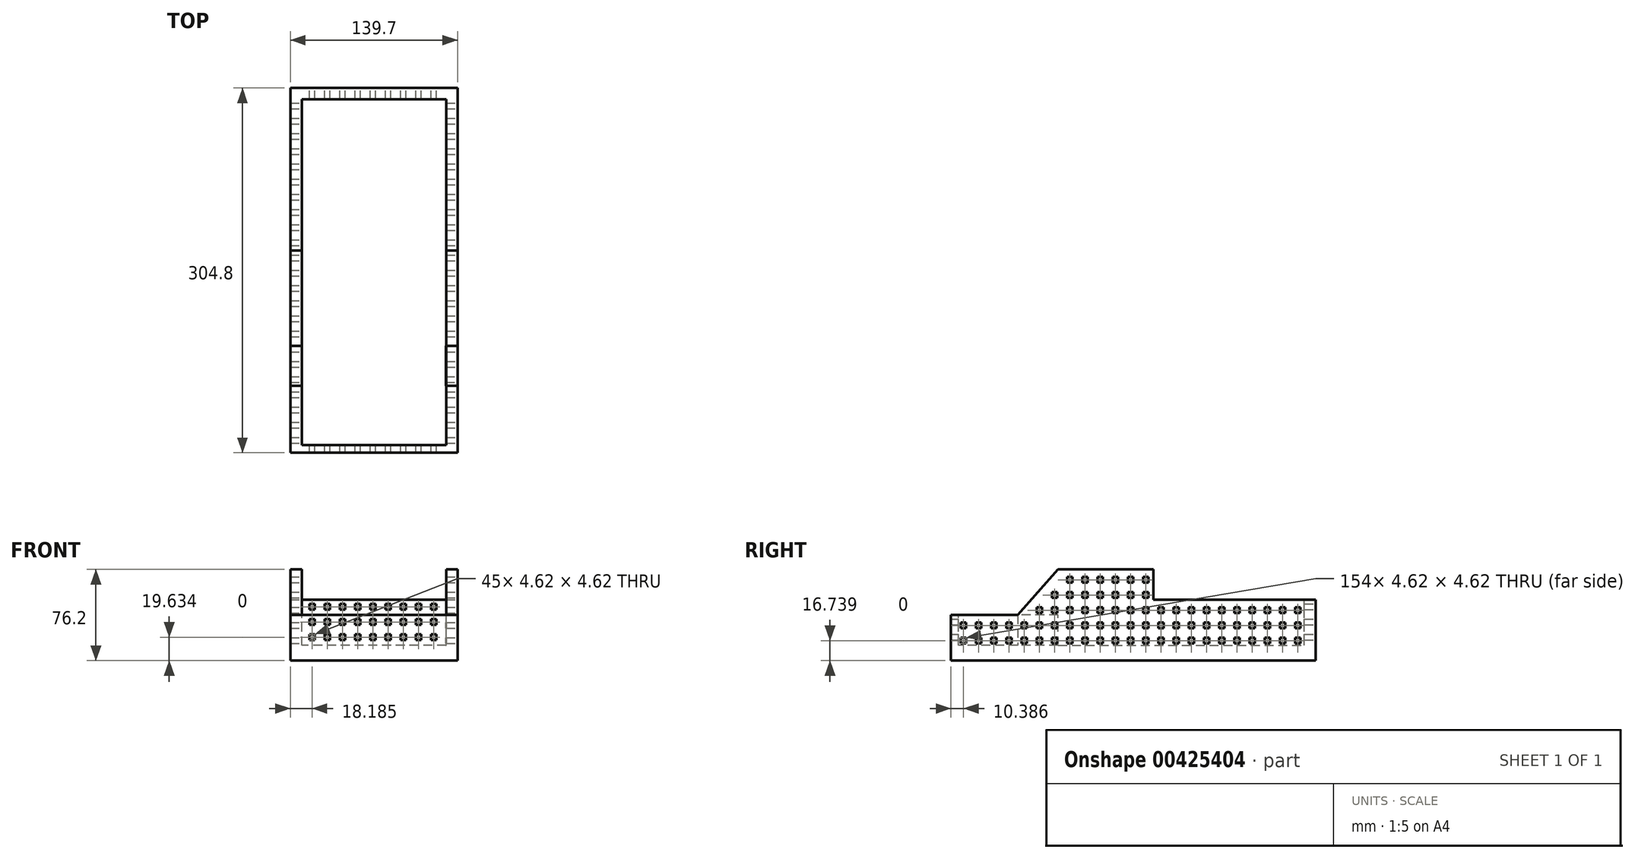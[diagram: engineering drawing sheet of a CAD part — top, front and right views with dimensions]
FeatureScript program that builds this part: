
annotation { "Feature Type Name" : "Feature", "Feature Type Description" : "" }
export const myFeature = defineFeature(function(context is Context, id is Id, definition is map)
    precondition{}
    {
        {
            var Q0;
            Q0=qCreatedBy(makeId("Top.planeOp"),FACE);
            var sketch = newSketch(context, id + "F0", { "sketchPlane" : qUnion([Q0])});
            skLineSegment(sketch, "E0.bottom", {"start": v(-57.73, 193.73) * mm, "end": v(81.97, 193.73) * mm});
            skLineSegment(sketch, "E0.top", {"start": v(-57.73, -111.07) * mm, "end": v(81.97, -111.07) * mm});
            skLineSegment(sketch, "E0.left", {"start": v(-57.73, 193.73) * mm, "end": v(-57.73, -111.07) * mm});
            skLineSegment(sketch, "E0.right", {"start": v(81.97, 193.73) * mm, "end": v(81.97, -111.07) * mm});
            skSolve(sketch);
        }
        {
            var Q0;
            Q0=makeQuery(id+"F0.imprint","IMPRINT",FACE,{"disambiguationData":[TD([[makeQuery(id+"F0.imprint","IMPRINT",EDGE,{"derivedFrom":sQuery(id+"F0.wireOp",EDGE,"E0.bottom")}),-1.0]])]});
            var Q1;
            Q1 = qSketchRegion(id + "F2", true);
            extrude(context, id + "F1", {"entities" : qUnion([Q0, Q1]), "oppositeDirection" : true, "depth" : 76.2 * mm});
        }
        {
            var Q0;
            Q0=makeQuery(id+"F1.opExtrude","SWEPT_FACE",FACE,{"disambiguationData":[OSD([sQuery(id+"F0.wireOp",EDGE,"E0.right")])]});
            var sketch = newSketch(context, id + "F2", { "sketchPlane" : qUnion([Q0])});
            skLineSegment(sketch, "E1", {"start": v(-111.07, -38.1) * mm, "end": v(-55.2, -38.1) * mm});
            skLineSegment(sketch, "E2", {"start": v(-55.2, -38.1) * mm, "end": v(-21.6, 0) * mm});
            skLineSegment(sketch, "E3", {"start": v(193.73, -25.4) * mm, "end": v(58.07, -25.4) * mm});
            skLineSegment(sketch, "E4", {"start": v(58.07, -25.4) * mm, "end": v(58.07, 0) * mm});
            skLineSegment(sketch, "E5", {"start": v(58.07, 0) * mm, "end": v(-21.6, 0) * mm});
            skSolve(sketch);
        }
        {
            var Q0;
            {var subQ0=sQuery(id+"F2.wireOp",EDGE,"E1");Q0=makeQuery(id+"F2.imprint","IMPRINT",FACE,{"disambiguationData":[TD([[makeQuery(id+"F2.imprint","IMPRINT",EDGE,{"derivedFrom":subQ0}),1.0]])]});}
            var Q1;
            {var subQ0=sQuery(id+"F2.wireOp",EDGE,"2gLDbXDt-uYVC-RE6O-0FNC-PgZezR3Lyq5D");Q1=makeQuery(id+"F2.imprint","IMPRINT",FACE,{"disambiguationData":[TD([[makeQuery(id+"F2.imprint","IMPRINT",EDGE,{"derivedFrom":subQ0}),-1.0]])]});}
            var Q2;
            {var subQ0=sQuery(id+"F2.wireOp",EDGE,"E3");Q2=makeQuery(id+"F2.imprint","IMPRINT",FACE,{"disambiguationData":[TD([[makeQuery(id+"F2.imprint","IMPRINT",EDGE,{"derivedFrom":subQ0}),-1.0]])]});}
            extrude(context, id + "F3", {"entities" : qUnion([Q0, Q1, Q2]), "operationType" : NewBodyOperationType.REMOVE, "endBound" : BoundingType.THROUGH_ALL, "oppositeDirection" : true, "depth" : 25.4 * mm});
        }
        {
            var Q0;
            Q0=makeQuery(id+"F3.boolean.opBoolean","COPY",FACE,{"derivedFrom":makeQuery(id+"F3.opExtrude","SWEPT_FACE",FACE,{"disambiguationData":[OSD([sQuery(id+"F2.wireOp",EDGE,"E3")])]})});
            var sketch = newSketch(context, id + "F4", { "sketchPlane" : qUnion([Q0])});
            skLineSegment(sketch, "E6.bottom", {"start": v(81.97, 58.07) * mm, "end": v(75.62, 58.07) * mm});
            skLineSegment(sketch, "E6.left", {"start": v(81.97, 58.07) * mm, "end": v(81.97, 64.42) * mm});
            skLineSegment(sketch, "E7.top", {"start": v(72.44, 184.2) * mm, "end": v(-48.2, 184.2) * mm});
            skLineSegment(sketch, "E7.left", {"start": v(72.44, 54.03) * mm, "end": v(72.44, 184.2) * mm});
            skLineSegment(sketch, "E7.right", {"start": v(-48.2, 54.03) * mm, "end": v(-48.2, 184.2) * mm});
            skSolve(sketch);
        }
        {
            var Q0;
            Q0=makeQuery(id+"F4.imprint","IMPRINT",FACE,{"disambiguationData":[TD([[makeQuery(id+"F4.imprint","IMPRINT",EDGE,{"derivedFrom":sQuery(id+"F4.wireOp",EDGE,"E7.bottom")}),-1.0]])]});
            var Q1;
            Q1=makeQuery(id+"F4.imprint","IMPRINT",FACE,{"disambiguationData":[TD([[makeQuery(id+"F4.imprint","IMPRINT",EDGE,{"derivedFrom":sQuery(id+"F4.wireOp",EDGE,"E7.top")}),1.0]])]});
            extrude(context, id + "F5", {"entities" : qUnion([Q0, Q1]), "operationType" : NewBodyOperationType.REMOVE, "oppositeDirection" : true, "depth" : 38.1 * mm});
        }
        {
            var Q0;
            Q0=makeQuery(id+"F1.opExtrude","CAP_FACE",FACE,{"disambiguationData":[OSD([sQuery(id+"F0.wireOp",EDGE,"E0.bottom"),sQuery(id+"F0.wireOp",EDGE,"E0.top"),sQuery(id+"F0.wireOp",EDGE,"E0.left"),sQuery(id+"F0.wireOp",EDGE,"E0.right")])],"isStart":true});
            var sketch = newSketch(context, id + "F6", { "sketchPlane" : qUnion([Q0])});
            skLineSegment(sketch, "E8.bottom", {"start": v(69.27, 58.07) * mm, "end": v(-45.03, 58.07) * mm});
            skLineSegment(sketch, "E8.top", {"start": v(69.27, -21.6) * mm, "end": v(-45.03, -21.6) * mm});
            skLineSegment(sketch, "E8.left", {"start": v(69.27, 58.07) * mm, "end": v(69.27, -21.6) * mm});
            skLineSegment(sketch, "E8.right", {"start": v(-45.03, 58.07) * mm, "end": v(-45.03, -21.6) * mm});
            skSolve(sketch);
        }
        {
            var Q0;
            Q0=makeQuery(id+"F6.imprint","IMPRINT",FACE,{"disambiguationData":[TD([[makeQuery(id+"F6.imprint","IMPRINT",EDGE,{"derivedFrom":sQuery(id+"F6.wireOp",EDGE,"E8.bottom")}),-1.0]])]});
            extrude(context, id + "F7", {"entities" : qUnion([Q0]), "operationType" : NewBodyOperationType.REMOVE, "oppositeDirection" : true, "depth" : 63.5 * mm});
        }
        {
            var Q0;
            Q0=makeQuery(id+"F3.boolean.opBoolean","COPY",FACE,{"derivedFrom":makeQuery(id+"F3.opExtrude","SWEPT_FACE",FACE,{"disambiguationData":[OSD([sQuery(id+"F2.wireOp",EDGE,"E1")])]})});
            var sketch = newSketch(context, id + "F8", { "sketchPlane" : qUnion([Q0])});
            skLineSegment(sketch, "E9.bottom", {"start": v(-57.73, -111.07) * mm, "end": v(-48.2, -111.07) * mm});
            skLineSegment(sketch, "E9.top", {"start": v(-57.73, -104.72) * mm, "end": v(-48.2, -104.72) * mm});
            skLineSegment(sketch, "E9.left", {"start": v(-57.73, -111.07) * mm, "end": v(-57.73, -104.72) * mm});
            skLineSegment(sketch, "E9.right", {"start": v(-48.2, -111.07) * mm, "end": v(-48.2, -104.72) * mm});
            skLineSegment(sketch, "E10.bottom", {"start": v(81.97, -55.2) * mm, "end": v(72.44, -55.2) * mm});
            skLineSegment(sketch, "E10.top", {"start": v(81.97, -61.54) * mm, "end": v(72.44, -61.54) * mm});
            skLineSegment(sketch, "E10.left", {"start": v(81.97, -55.2) * mm, "end": v(81.97, -61.54) * mm});
            skLineSegment(sketch, "E10.right", {"start": v(72.44, -55.2) * mm, "end": v(72.44, -61.54) * mm});
            skLineSegment(sketch, "E11.top", {"start": v(72.44, -104.72) * mm, "end": v(-48.2, -104.72) * mm});
            skLineSegment(sketch, "E11.left", {"start": v(72.44, -61.54) * mm, "end": v(72.44, -104.72) * mm});
            skLineSegment(sketch, "E11.right", {"start": v(-48.2, -61.54) * mm, "end": v(-48.2, -104.72) * mm});
            skLineSegment(sketch, "E12", {"start": v(-48.2, -61.54) * mm, "end": v(-48.2, -55.2) * mm});
            skSolve(sketch);
        }
        {
            var Q0;
            Q0=makeQuery(id+"F8.imprint","IMPRINT",FACE,{"disambiguationData":[TD([[makeQuery(id+"F8.imprint","IMPRINT",EDGE,{"derivedFrom":sQuery(id+"F8.wireOp",EDGE,"E11.bottom")}),1.0]])]});
            var Q1;
            {var subQ0=sQuery(id+"F8.wireOp",EDGE,"E10.right");Q1=makeQuery(id+"F8.imprint","IMPRINT",FACE,{"disambiguationData":[TD([[makeQuery(id+"F8.imprint","IMPRINT",EDGE,{"derivedFrom":subQ0}),-1.0]])]});}
            extrude(context, id + "F9", {"entities" : qUnion([Q0, Q1]), "operationType" : NewBodyOperationType.REMOVE, "oppositeDirection" : true, "depth" : 25.4 * mm});
        }
        {
            var Q0;
            Q0=makeQuery(id+"F1.opExtrude","SWEPT_FACE",FACE,{"disambiguationData":[OSD([sQuery(id+"F0.wireOp",EDGE,"E0.right")])]});
            var sketch = newSketch(context, id + "F10", { "sketchPlane" : qUnion([Q0])});
            skLineSegment(sketch, "E13.bottom", {"start": v(-111.07, -76.2) * mm, "end": v(-103, -76.2) * mm});
            skLineSegment(sketch, "E13.top", {"start": v(-111.07, -61.77) * mm, "end": v(-103, -61.77) * mm});
            skLineSegment(sketch, "E13.left", {"start": v(-111.07, -76.2) * mm, "end": v(-111.07, -61.77) * mm});
            skLineSegment(sketch, "E13.right", {"start": v(-103, -76.2) * mm, "end": v(-103, -61.77) * mm});
            skLineSegment(sketch, "E14.bottom", {"start": v(-103, -61.77) * mm, "end": v(-98.37, -61.77) * mm});
            skLineSegment(sketch, "E14.top", {"start": v(-103, -57.15) * mm, "end": v(-98.37, -57.15) * mm});
            skLineSegment(sketch, "E14.left", {"start": v(-103, -61.77) * mm, "end": v(-103, -57.15) * mm});
            skLineSegment(sketch, "E14.right", {"start": v(-98.37, -61.77) * mm, "end": v(-98.37, -57.15) * mm});
            skLineSegment(sketch, "E15.0.1.0", {"start": v(-98.37, -49.07) * mm, "end": v(-98.37, -44.45) * mm});
            skLineSegment(sketch, "E15.0.1.1", {"start": v(-103, -44.45) * mm, "end": v(-98.37, -44.45) * mm});
            skLineSegment(sketch, "E15.0.1.2", {"start": v(-103, -49.07) * mm, "end": v(-103, -44.45) * mm});
            skLineSegment(sketch, "E15.0.1.3", {"start": v(-103, -49.07) * mm, "end": v(-98.37, -49.07) * mm});
            skLineSegment(sketch, "E15.1.0.0", {"start": v(-85.67, -61.77) * mm, "end": v(-85.67, -57.15) * mm});
            skLineSegment(sketch, "E15.1.0.1", {"start": v(-90.3, -57.15) * mm, "end": v(-85.67, -57.15) * mm});
            skLineSegment(sketch, "E15.1.0.2", {"start": v(-90.3, -61.77) * mm, "end": v(-90.3, -57.15) * mm});
            skLineSegment(sketch, "E15.1.0.3", {"start": v(-90.3, -61.77) * mm, "end": v(-85.67, -61.77) * mm});
            skLineSegment(sketch, "E15.1.1.0", {"start": v(-85.67, -49.07) * mm, "end": v(-85.67, -44.45) * mm});
            skLineSegment(sketch, "E15.1.1.1", {"start": v(-90.3, -44.45) * mm, "end": v(-85.67, -44.45) * mm});
            skLineSegment(sketch, "E15.1.1.2", {"start": v(-90.3, -49.07) * mm, "end": v(-90.3, -44.45) * mm});
            skLineSegment(sketch, "E15.1.1.3", {"start": v(-90.3, -49.07) * mm, "end": v(-85.67, -49.07) * mm});
            skLineSegment(sketch, "E15.2.0.0", {"start": v(-72.97, -61.77) * mm, "end": v(-72.97, -57.15) * mm});
            skLineSegment(sketch, "E15.2.0.1", {"start": v(-77.6, -57.15) * mm, "end": v(-72.97, -57.15) * mm});
            skLineSegment(sketch, "E15.2.0.2", {"start": v(-77.6, -61.77) * mm, "end": v(-77.6, -57.15) * mm});
            skLineSegment(sketch, "E15.2.0.3", {"start": v(-77.6, -61.77) * mm, "end": v(-72.97, -61.77) * mm});
            skLineSegment(sketch, "E15.2.1.0", {"start": v(-72.97, -49.07) * mm, "end": v(-72.97, -44.45) * mm});
            skLineSegment(sketch, "E15.2.1.1", {"start": v(-77.6, -44.45) * mm, "end": v(-72.97, -44.45) * mm});
            skLineSegment(sketch, "E15.2.1.2", {"start": v(-77.6, -49.07) * mm, "end": v(-77.6, -44.45) * mm});
            skLineSegment(sketch, "E15.2.1.3", {"start": v(-77.6, -49.07) * mm, "end": v(-72.97, -49.07) * mm});
            skLineSegment(sketch, "E15.3.0.0", {"start": v(-60.27, -61.77) * mm, "end": v(-60.27, -57.15) * mm});
            skLineSegment(sketch, "E15.3.0.1", {"start": v(-64.9, -57.15) * mm, "end": v(-60.27, -57.15) * mm});
            skLineSegment(sketch, "E15.3.0.2", {"start": v(-64.9, -61.77) * mm, "end": v(-64.9, -57.15) * mm});
            skLineSegment(sketch, "E15.3.0.3", {"start": v(-64.9, -61.77) * mm, "end": v(-60.27, -61.77) * mm});
            skLineSegment(sketch, "E15.3.1.0", {"start": v(-60.27, -49.07) * mm, "end": v(-60.27, -44.45) * mm});
            skLineSegment(sketch, "E15.3.1.1", {"start": v(-64.9, -44.45) * mm, "end": v(-60.27, -44.45) * mm});
            skLineSegment(sketch, "E15.3.1.2", {"start": v(-64.9, -49.07) * mm, "end": v(-64.9, -44.45) * mm});
            skLineSegment(sketch, "E15.3.1.3", {"start": v(-64.9, -49.07) * mm, "end": v(-60.27, -49.07) * mm});
            skLineSegment(sketch, "E15.4.0.0", {"start": v(-47.57, -61.77) * mm, "end": v(-47.57, -57.15) * mm});
            skLineSegment(sketch, "E15.4.0.1", {"start": v(-52.2, -57.15) * mm, "end": v(-47.57, -57.15) * mm});
            skLineSegment(sketch, "E15.4.0.2", {"start": v(-52.2, -61.77) * mm, "end": v(-52.2, -57.15) * mm});
            skLineSegment(sketch, "E15.4.0.3", {"start": v(-52.2, -61.77) * mm, "end": v(-47.57, -61.77) * mm});
            skLineSegment(sketch, "E15.4.1.0", {"start": v(-47.57, -49.07) * mm, "end": v(-47.57, -44.45) * mm});
            skLineSegment(sketch, "E15.4.1.1", {"start": v(-52.2, -44.45) * mm, "end": v(-47.57, -44.45) * mm});
            skLineSegment(sketch, "E15.4.1.2", {"start": v(-52.2, -49.07) * mm, "end": v(-52.2, -44.45) * mm});
            skLineSegment(sketch, "E15.4.1.3", {"start": v(-52.2, -49.07) * mm, "end": v(-47.57, -49.07) * mm});
            skLineSegment(sketch, "E15.5.0.0", {"start": v(-34.87, -61.77) * mm, "end": v(-34.87, -57.15) * mm});
            skLineSegment(sketch, "E15.5.0.1", {"start": v(-39.5, -57.15) * mm, "end": v(-34.87, -57.15) * mm});
            skLineSegment(sketch, "E15.5.0.2", {"start": v(-39.5, -61.77) * mm, "end": v(-39.5, -57.15) * mm});
            skLineSegment(sketch, "E15.5.0.3", {"start": v(-39.5, -61.77) * mm, "end": v(-34.87, -61.77) * mm});
            skLineSegment(sketch, "E15.5.1.0", {"start": v(-34.87, -49.07) * mm, "end": v(-34.87, -44.45) * mm});
            skLineSegment(sketch, "E15.5.1.1", {"start": v(-39.5, -44.45) * mm, "end": v(-34.87, -44.45) * mm});
            skLineSegment(sketch, "E15.5.1.2", {"start": v(-39.5, -49.07) * mm, "end": v(-39.5, -44.45) * mm});
            skLineSegment(sketch, "E15.5.1.3", {"start": v(-39.5, -49.07) * mm, "end": v(-34.87, -49.07) * mm});
            skLineSegment(sketch, "E15.5.2.0", {"start": v(-34.87, -36.37) * mm, "end": v(-34.87, -31.75) * mm});
            skLineSegment(sketch, "E15.5.2.1", {"start": v(-39.5, -31.75) * mm, "end": v(-34.87, -31.75) * mm});
            skLineSegment(sketch, "E15.5.2.2", {"start": v(-39.5, -36.37) * mm, "end": v(-39.5, -31.75) * mm});
            skLineSegment(sketch, "E15.5.2.3", {"start": v(-39.5, -36.37) * mm, "end": v(-34.87, -36.37) * mm});
            skLineSegment(sketch, "E15.6.0.0", {"start": v(-22.17, -61.77) * mm, "end": v(-22.17, -57.15) * mm});
            skLineSegment(sketch, "E15.6.0.1", {"start": v(-26.8, -57.15) * mm, "end": v(-22.17, -57.15) * mm});
            skLineSegment(sketch, "E15.6.0.2", {"start": v(-26.8, -61.77) * mm, "end": v(-26.8, -57.15) * mm});
            skLineSegment(sketch, "E15.6.0.3", {"start": v(-26.8, -61.77) * mm, "end": v(-22.17, -61.77) * mm});
            skLineSegment(sketch, "E15.6.1.0", {"start": v(-22.17, -49.07) * mm, "end": v(-22.17, -44.45) * mm});
            skLineSegment(sketch, "E15.6.1.1", {"start": v(-26.8, -44.45) * mm, "end": v(-22.17, -44.45) * mm});
            skLineSegment(sketch, "E15.6.1.2", {"start": v(-26.8, -49.07) * mm, "end": v(-26.8, -44.45) * mm});
            skLineSegment(sketch, "E15.6.1.3", {"start": v(-26.8, -49.07) * mm, "end": v(-22.17, -49.07) * mm});
            skLineSegment(sketch, "E15.6.2.0", {"start": v(-22.17, -36.37) * mm, "end": v(-22.17, -31.75) * mm});
            skLineSegment(sketch, "E15.6.2.1", {"start": v(-26.8, -31.75) * mm, "end": v(-22.17, -31.75) * mm});
            skLineSegment(sketch, "E15.6.2.2", {"start": v(-26.8, -36.37) * mm, "end": v(-26.8, -31.75) * mm});
            skLineSegment(sketch, "E15.6.2.3", {"start": v(-26.8, -36.37) * mm, "end": v(-22.17, -36.37) * mm});
            skLineSegment(sketch, "E15.6.3.0", {"start": v(-22.17, -23.67) * mm, "end": v(-22.17, -19.05) * mm});
            skLineSegment(sketch, "E15.6.3.1", {"start": v(-26.8, -19.05) * mm, "end": v(-22.17, -19.05) * mm});
            skLineSegment(sketch, "E15.6.3.2", {"start": v(-26.8, -23.67) * mm, "end": v(-26.8, -19.05) * mm});
            skLineSegment(sketch, "E15.6.3.3", {"start": v(-26.8, -23.67) * mm, "end": v(-22.17, -23.67) * mm});
            skLineSegment(sketch, "E15.7.0.0", {"start": v(-9.47, -61.77) * mm, "end": v(-9.47, -57.15) * mm});
            skLineSegment(sketch, "E15.7.0.1", {"start": v(-14.1, -57.15) * mm, "end": v(-9.47, -57.15) * mm});
            skLineSegment(sketch, "E15.7.0.2", {"start": v(-14.1, -61.77) * mm, "end": v(-14.1, -57.15) * mm});
            skLineSegment(sketch, "E15.7.0.3", {"start": v(-14.1, -61.77) * mm, "end": v(-9.47, -61.77) * mm});
            skLineSegment(sketch, "E15.7.1.0", {"start": v(-9.47, -49.07) * mm, "end": v(-9.47, -44.45) * mm});
            skLineSegment(sketch, "E15.7.1.1", {"start": v(-14.1, -44.45) * mm, "end": v(-9.47, -44.45) * mm});
            skLineSegment(sketch, "E15.7.1.2", {"start": v(-14.1, -49.07) * mm, "end": v(-14.1, -44.45) * mm});
            skLineSegment(sketch, "E15.7.1.3", {"start": v(-14.1, -49.07) * mm, "end": v(-9.47, -49.07) * mm});
            skLineSegment(sketch, "E15.7.2.0", {"start": v(-9.47, -36.37) * mm, "end": v(-9.47, -31.75) * mm});
            skLineSegment(sketch, "E15.7.2.1", {"start": v(-14.1, -31.75) * mm, "end": v(-9.47, -31.75) * mm});
            skLineSegment(sketch, "E15.7.2.2", {"start": v(-14.1, -36.37) * mm, "end": v(-14.1, -31.75) * mm});
            skLineSegment(sketch, "E15.7.2.3", {"start": v(-14.1, -36.37) * mm, "end": v(-9.47, -36.37) * mm});
            skLineSegment(sketch, "E15.7.3.0", {"start": v(-9.47, -23.67) * mm, "end": v(-9.47, -19.05) * mm});
            skLineSegment(sketch, "E15.7.3.1", {"start": v(-14.1, -19.05) * mm, "end": v(-9.47, -19.05) * mm});
            skLineSegment(sketch, "E15.7.3.2", {"start": v(-14.1, -23.67) * mm, "end": v(-14.1, -19.05) * mm});
            skLineSegment(sketch, "E15.7.3.3", {"start": v(-14.1, -23.67) * mm, "end": v(-9.47, -23.67) * mm});
            skLineSegment(sketch, "E15.7.4.0", {"start": v(-9.47, -10.97) * mm, "end": v(-9.47, -6.35) * mm});
            skLineSegment(sketch, "E15.7.4.1", {"start": v(-14.1, -6.35) * mm, "end": v(-9.47, -6.35) * mm});
            skLineSegment(sketch, "E15.7.4.2", {"start": v(-14.1, -10.97) * mm, "end": v(-14.1, -6.35) * mm});
            skLineSegment(sketch, "E15.7.4.3", {"start": v(-14.1, -10.97) * mm, "end": v(-9.47, -10.97) * mm});
            skLineSegment(sketch, "E15.8.0.0", {"start": v(3.23, -61.77) * mm, "end": v(3.23, -57.15) * mm});
            skLineSegment(sketch, "E15.8.0.1", {"start": v(-1.4, -57.15) * mm, "end": v(3.23, -57.15) * mm});
            skLineSegment(sketch, "E15.8.0.2", {"start": v(-1.4, -61.77) * mm, "end": v(-1.4, -57.15) * mm});
            skLineSegment(sketch, "E15.8.0.3", {"start": v(-1.4, -61.77) * mm, "end": v(3.23, -61.77) * mm});
            skLineSegment(sketch, "E15.8.1.0", {"start": v(3.23, -49.07) * mm, "end": v(3.23, -44.45) * mm});
            skLineSegment(sketch, "E15.8.1.1", {"start": v(-1.4, -44.45) * mm, "end": v(3.23, -44.45) * mm});
            skLineSegment(sketch, "E15.8.1.2", {"start": v(-1.4, -49.07) * mm, "end": v(-1.4, -44.45) * mm});
            skLineSegment(sketch, "E15.8.1.3", {"start": v(-1.4, -49.07) * mm, "end": v(3.23, -49.07) * mm});
            skLineSegment(sketch, "E15.8.2.0", {"start": v(3.23, -36.37) * mm, "end": v(3.23, -31.75) * mm});
            skLineSegment(sketch, "E15.8.2.1", {"start": v(-1.4, -31.75) * mm, "end": v(3.23, -31.75) * mm});
            skLineSegment(sketch, "E15.8.2.2", {"start": v(-1.4, -36.37) * mm, "end": v(-1.4, -31.75) * mm});
            skLineSegment(sketch, "E15.8.2.3", {"start": v(-1.4, -36.37) * mm, "end": v(3.23, -36.37) * mm});
            skLineSegment(sketch, "E15.8.3.0", {"start": v(3.23, -23.67) * mm, "end": v(3.23, -19.05) * mm});
            skLineSegment(sketch, "E15.8.3.1", {"start": v(-1.4, -19.05) * mm, "end": v(3.23, -19.05) * mm});
            skLineSegment(sketch, "E15.8.3.2", {"start": v(-1.4, -23.67) * mm, "end": v(-1.4, -19.05) * mm});
            skLineSegment(sketch, "E15.8.3.3", {"start": v(-1.4, -23.67) * mm, "end": v(3.23, -23.67) * mm});
            skLineSegment(sketch, "E15.8.4.0", {"start": v(3.23, -10.97) * mm, "end": v(3.23, -6.35) * mm});
            skLineSegment(sketch, "E15.8.4.1", {"start": v(-1.4, -6.35) * mm, "end": v(3.23, -6.35) * mm});
            skLineSegment(sketch, "E15.8.4.2", {"start": v(-1.4, -10.97) * mm, "end": v(-1.4, -6.35) * mm});
            skLineSegment(sketch, "E15.8.4.3", {"start": v(-1.4, -10.97) * mm, "end": v(3.23, -10.97) * mm});
            skLineSegment(sketch, "E15.9.0.0", {"start": v(15.93, -61.77) * mm, "end": v(15.93, -57.15) * mm});
            skLineSegment(sketch, "E15.9.0.1", {"start": v(11.3, -57.15) * mm, "end": v(15.93, -57.15) * mm});
            skLineSegment(sketch, "E15.9.0.2", {"start": v(11.3, -61.77) * mm, "end": v(11.3, -57.15) * mm});
            skLineSegment(sketch, "E15.9.0.3", {"start": v(11.3, -61.77) * mm, "end": v(15.93, -61.77) * mm});
            skLineSegment(sketch, "E15.9.1.0", {"start": v(15.93, -49.07) * mm, "end": v(15.93, -44.45) * mm});
            skLineSegment(sketch, "E15.9.1.1", {"start": v(11.3, -44.45) * mm, "end": v(15.93, -44.45) * mm});
            skLineSegment(sketch, "E15.9.1.2", {"start": v(11.3, -49.07) * mm, "end": v(11.3, -44.45) * mm});
            skLineSegment(sketch, "E15.9.1.3", {"start": v(11.3, -49.07) * mm, "end": v(15.93, -49.07) * mm});
            skLineSegment(sketch, "E15.9.2.0", {"start": v(15.93, -36.37) * mm, "end": v(15.93, -31.75) * mm});
            skLineSegment(sketch, "E15.9.2.1", {"start": v(11.3, -31.75) * mm, "end": v(15.93, -31.75) * mm});
            skLineSegment(sketch, "E15.9.2.2", {"start": v(11.3, -36.37) * mm, "end": v(11.3, -31.75) * mm});
            skLineSegment(sketch, "E15.9.2.3", {"start": v(11.3, -36.37) * mm, "end": v(15.93, -36.37) * mm});
            skLineSegment(sketch, "E15.9.3.0", {"start": v(15.93, -23.67) * mm, "end": v(15.93, -19.05) * mm});
            skLineSegment(sketch, "E15.9.3.1", {"start": v(11.3, -19.05) * mm, "end": v(15.93, -19.05) * mm});
            skLineSegment(sketch, "E15.9.3.2", {"start": v(11.3, -23.67) * mm, "end": v(11.3, -19.05) * mm});
            skLineSegment(sketch, "E15.9.3.3", {"start": v(11.3, -23.67) * mm, "end": v(15.93, -23.67) * mm});
            skLineSegment(sketch, "E15.9.4.0", {"start": v(15.93, -10.97) * mm, "end": v(15.93, -6.35) * mm});
            skLineSegment(sketch, "E15.9.4.1", {"start": v(11.3, -6.35) * mm, "end": v(15.93, -6.35) * mm});
            skLineSegment(sketch, "E15.9.4.2", {"start": v(11.3, -10.97) * mm, "end": v(11.3, -6.35) * mm});
            skLineSegment(sketch, "E15.9.4.3", {"start": v(11.3, -10.97) * mm, "end": v(15.93, -10.97) * mm});
            skLineSegment(sketch, "E15.10.0.0", {"start": v(28.63, -61.77) * mm, "end": v(28.63, -57.15) * mm});
            skLineSegment(sketch, "E15.10.0.1", {"start": v(24, -57.15) * mm, "end": v(28.63, -57.15) * mm});
            skLineSegment(sketch, "E15.10.0.2", {"start": v(24, -61.77) * mm, "end": v(24, -57.15) * mm});
            skLineSegment(sketch, "E15.10.0.3", {"start": v(24, -61.77) * mm, "end": v(28.63, -61.77) * mm});
            skLineSegment(sketch, "E15.10.1.0", {"start": v(28.63, -49.07) * mm, "end": v(28.63, -44.45) * mm});
            skLineSegment(sketch, "E15.10.1.1", {"start": v(24, -44.45) * mm, "end": v(28.63, -44.45) * mm});
            skLineSegment(sketch, "E15.10.1.2", {"start": v(24, -49.07) * mm, "end": v(24, -44.45) * mm});
            skLineSegment(sketch, "E15.10.1.3", {"start": v(24, -49.07) * mm, "end": v(28.63, -49.07) * mm});
            skLineSegment(sketch, "E15.10.2.0", {"start": v(28.63, -36.37) * mm, "end": v(28.63, -31.75) * mm});
            skLineSegment(sketch, "E15.10.2.1", {"start": v(24, -31.75) * mm, "end": v(28.63, -31.75) * mm});
            skLineSegment(sketch, "E15.10.2.2", {"start": v(24, -36.37) * mm, "end": v(24, -31.75) * mm});
            skLineSegment(sketch, "E15.10.2.3", {"start": v(24, -36.37) * mm, "end": v(28.63, -36.37) * mm});
            skLineSegment(sketch, "E15.10.3.0", {"start": v(28.63, -23.67) * mm, "end": v(28.63, -19.05) * mm});
            skLineSegment(sketch, "E15.10.3.1", {"start": v(24, -19.05) * mm, "end": v(28.63, -19.05) * mm});
            skLineSegment(sketch, "E15.10.3.2", {"start": v(24, -23.67) * mm, "end": v(24, -19.05) * mm});
            skLineSegment(sketch, "E15.10.3.3", {"start": v(24, -23.67) * mm, "end": v(28.63, -23.67) * mm});
            skLineSegment(sketch, "E15.10.4.0", {"start": v(28.63, -10.97) * mm, "end": v(28.63, -6.35) * mm});
            skLineSegment(sketch, "E15.10.4.1", {"start": v(24, -6.35) * mm, "end": v(28.63, -6.35) * mm});
            skLineSegment(sketch, "E15.10.4.2", {"start": v(24, -10.97) * mm, "end": v(24, -6.35) * mm});
            skLineSegment(sketch, "E15.10.4.3", {"start": v(24, -10.97) * mm, "end": v(28.63, -10.97) * mm});
            skLineSegment(sketch, "E15.11.0.0", {"start": v(41.33, -61.77) * mm, "end": v(41.33, -57.15) * mm});
            skLineSegment(sketch, "E15.11.0.1", {"start": v(36.7, -57.15) * mm, "end": v(41.33, -57.15) * mm});
            skLineSegment(sketch, "E15.11.0.2", {"start": v(36.7, -61.77) * mm, "end": v(36.7, -57.15) * mm});
            skLineSegment(sketch, "E15.11.0.3", {"start": v(36.7, -61.77) * mm, "end": v(41.33, -61.77) * mm});
            skLineSegment(sketch, "E15.11.1.0", {"start": v(41.33, -49.07) * mm, "end": v(41.33, -44.45) * mm});
            skLineSegment(sketch, "E15.11.1.1", {"start": v(36.7, -44.45) * mm, "end": v(41.33, -44.45) * mm});
            skLineSegment(sketch, "E15.11.1.2", {"start": v(36.7, -49.07) * mm, "end": v(36.7, -44.45) * mm});
            skLineSegment(sketch, "E15.11.1.3", {"start": v(36.7, -49.07) * mm, "end": v(41.33, -49.07) * mm});
            skLineSegment(sketch, "E15.11.2.0", {"start": v(41.33, -36.37) * mm, "end": v(41.33, -31.75) * mm});
            skLineSegment(sketch, "E15.11.2.1", {"start": v(36.7, -31.75) * mm, "end": v(41.33, -31.75) * mm});
            skLineSegment(sketch, "E15.11.2.2", {"start": v(36.7, -36.37) * mm, "end": v(36.7, -31.75) * mm});
            skLineSegment(sketch, "E15.11.2.3", {"start": v(36.7, -36.37) * mm, "end": v(41.33, -36.37) * mm});
            skLineSegment(sketch, "E15.11.3.0", {"start": v(41.33, -23.67) * mm, "end": v(41.33, -19.05) * mm});
            skLineSegment(sketch, "E15.11.3.1", {"start": v(36.7, -19.05) * mm, "end": v(41.33, -19.05) * mm});
            skLineSegment(sketch, "E15.11.3.2", {"start": v(36.7, -23.67) * mm, "end": v(36.7, -19.05) * mm});
            skLineSegment(sketch, "E15.11.3.3", {"start": v(36.7, -23.67) * mm, "end": v(41.33, -23.67) * mm});
            skLineSegment(sketch, "E15.11.4.0", {"start": v(41.33, -10.97) * mm, "end": v(41.33, -6.35) * mm});
            skLineSegment(sketch, "E15.11.4.1", {"start": v(36.7, -6.35) * mm, "end": v(41.33, -6.35) * mm});
            skLineSegment(sketch, "E15.11.4.2", {"start": v(36.7, -10.97) * mm, "end": v(36.7, -6.35) * mm});
            skLineSegment(sketch, "E15.11.4.3", {"start": v(36.7, -10.97) * mm, "end": v(41.33, -10.97) * mm});
            skLineSegment(sketch, "E15.12.0.0", {"start": v(54.03, -61.77) * mm, "end": v(54.03, -57.15) * mm});
            skLineSegment(sketch, "E15.12.0.1", {"start": v(49.4, -57.15) * mm, "end": v(54.03, -57.15) * mm});
            skLineSegment(sketch, "E15.12.0.2", {"start": v(49.4, -61.77) * mm, "end": v(49.4, -57.15) * mm});
            skLineSegment(sketch, "E15.12.0.3", {"start": v(49.4, -61.77) * mm, "end": v(54.03, -61.77) * mm});
            skLineSegment(sketch, "E15.12.1.0", {"start": v(54.03, -49.07) * mm, "end": v(54.03, -44.45) * mm});
            skLineSegment(sketch, "E15.12.1.1", {"start": v(49.4, -44.45) * mm, "end": v(54.03, -44.45) * mm});
            skLineSegment(sketch, "E15.12.1.2", {"start": v(49.4, -49.07) * mm, "end": v(49.4, -44.45) * mm});
            skLineSegment(sketch, "E15.12.1.3", {"start": v(49.4, -49.07) * mm, "end": v(54.03, -49.07) * mm});
            skLineSegment(sketch, "E15.12.2.0", {"start": v(54.03, -36.37) * mm, "end": v(54.03, -31.75) * mm});
            skLineSegment(sketch, "E15.12.2.1", {"start": v(49.4, -31.75) * mm, "end": v(54.03, -31.75) * mm});
            skLineSegment(sketch, "E15.12.2.2", {"start": v(49.4, -36.37) * mm, "end": v(49.4, -31.75) * mm});
            skLineSegment(sketch, "E15.12.2.3", {"start": v(49.4, -36.37) * mm, "end": v(54.03, -36.37) * mm});
            skLineSegment(sketch, "E15.13.0.0", {"start": v(66.73, -61.77) * mm, "end": v(66.73, -57.15) * mm});
            skLineSegment(sketch, "E15.13.0.1", {"start": v(62.1, -57.15) * mm, "end": v(66.73, -57.15) * mm});
            skLineSegment(sketch, "E15.13.0.2", {"start": v(62.1, -61.77) * mm, "end": v(62.1, -57.15) * mm});
            skLineSegment(sketch, "E15.13.0.3", {"start": v(62.1, -61.77) * mm, "end": v(66.73, -61.77) * mm});
            skLineSegment(sketch, "E15.13.1.0", {"start": v(66.73, -49.07) * mm, "end": v(66.73, -44.45) * mm});
            skLineSegment(sketch, "E15.13.1.1", {"start": v(62.1, -44.45) * mm, "end": v(66.73, -44.45) * mm});
            skLineSegment(sketch, "E15.13.1.2", {"start": v(62.1, -49.07) * mm, "end": v(62.1, -44.45) * mm});
            skLineSegment(sketch, "E15.13.1.3", {"start": v(62.1, -49.07) * mm, "end": v(66.73, -49.07) * mm});
            skLineSegment(sketch, "E15.13.2.0", {"start": v(66.73, -36.37) * mm, "end": v(66.73, -31.75) * mm});
            skLineSegment(sketch, "E15.13.2.1", {"start": v(62.1, -31.75) * mm, "end": v(66.73, -31.75) * mm});
            skLineSegment(sketch, "E15.13.2.2", {"start": v(62.1, -36.37) * mm, "end": v(62.1, -31.75) * mm});
            skLineSegment(sketch, "E15.13.2.3", {"start": v(62.1, -36.37) * mm, "end": v(66.73, -36.37) * mm});
            skLineSegment(sketch, "E15.14.0.0", {"start": v(79.43, -61.77) * mm, "end": v(79.43, -57.15) * mm});
            skLineSegment(sketch, "E15.14.0.1", {"start": v(74.8, -57.15) * mm, "end": v(79.43, -57.15) * mm});
            skLineSegment(sketch, "E15.14.0.2", {"start": v(74.8, -61.77) * mm, "end": v(74.8, -57.15) * mm});
            skLineSegment(sketch, "E15.14.0.3", {"start": v(74.8, -61.77) * mm, "end": v(79.43, -61.77) * mm});
            skLineSegment(sketch, "E15.14.1.0", {"start": v(79.43, -49.07) * mm, "end": v(79.43, -44.45) * mm});
            skLineSegment(sketch, "E15.14.1.1", {"start": v(74.8, -44.45) * mm, "end": v(79.43, -44.45) * mm});
            skLineSegment(sketch, "E15.14.1.2", {"start": v(74.8, -49.07) * mm, "end": v(74.8, -44.45) * mm});
            skLineSegment(sketch, "E15.14.1.3", {"start": v(74.8, -49.07) * mm, "end": v(79.43, -49.07) * mm});
            skLineSegment(sketch, "E15.14.2.0", {"start": v(79.43, -36.37) * mm, "end": v(79.43, -31.75) * mm});
            skLineSegment(sketch, "E15.14.2.1", {"start": v(74.8, -31.75) * mm, "end": v(79.43, -31.75) * mm});
            skLineSegment(sketch, "E15.14.2.2", {"start": v(74.8, -36.37) * mm, "end": v(74.8, -31.75) * mm});
            skLineSegment(sketch, "E15.14.2.3", {"start": v(74.8, -36.37) * mm, "end": v(79.43, -36.37) * mm});
            skLineSegment(sketch, "E15.15.0.0", {"start": v(92.13, -61.77) * mm, "end": v(92.13, -57.15) * mm});
            skLineSegment(sketch, "E15.15.0.1", {"start": v(87.5, -57.15) * mm, "end": v(92.13, -57.15) * mm});
            skLineSegment(sketch, "E15.15.0.2", {"start": v(87.5, -61.77) * mm, "end": v(87.5, -57.15) * mm});
            skLineSegment(sketch, "E15.15.0.3", {"start": v(87.5, -61.77) * mm, "end": v(92.13, -61.77) * mm});
            skLineSegment(sketch, "E15.15.1.0", {"start": v(92.13, -49.07) * mm, "end": v(92.13, -44.45) * mm});
            skLineSegment(sketch, "E15.15.1.1", {"start": v(87.5, -44.45) * mm, "end": v(92.13, -44.45) * mm});
            skLineSegment(sketch, "E15.15.1.2", {"start": v(87.5, -49.07) * mm, "end": v(87.5, -44.45) * mm});
            skLineSegment(sketch, "E15.15.1.3", {"start": v(87.5, -49.07) * mm, "end": v(92.13, -49.07) * mm});
            skLineSegment(sketch, "E15.15.2.0", {"start": v(92.13, -36.37) * mm, "end": v(92.13, -31.75) * mm});
            skLineSegment(sketch, "E15.15.2.1", {"start": v(87.5, -31.75) * mm, "end": v(92.13, -31.75) * mm});
            skLineSegment(sketch, "E15.15.2.2", {"start": v(87.5, -36.37) * mm, "end": v(87.5, -31.75) * mm});
            skLineSegment(sketch, "E15.15.2.3", {"start": v(87.5, -36.37) * mm, "end": v(92.13, -36.37) * mm});
            skLineSegment(sketch, "E15.16.0.0", {"start": v(104.83, -61.77) * mm, "end": v(104.83, -57.15) * mm});
            skLineSegment(sketch, "E15.16.0.1", {"start": v(100.2, -57.15) * mm, "end": v(104.83, -57.15) * mm});
            skLineSegment(sketch, "E15.16.0.2", {"start": v(100.2, -61.77) * mm, "end": v(100.2, -57.15) * mm});
            skLineSegment(sketch, "E15.16.0.3", {"start": v(100.2, -61.77) * mm, "end": v(104.83, -61.77) * mm});
            skLineSegment(sketch, "E15.16.1.0", {"start": v(104.83, -49.07) * mm, "end": v(104.83, -44.45) * mm});
            skLineSegment(sketch, "E15.16.1.1", {"start": v(100.2, -44.45) * mm, "end": v(104.83, -44.45) * mm});
            skLineSegment(sketch, "E15.16.1.2", {"start": v(100.2, -49.07) * mm, "end": v(100.2, -44.45) * mm});
            skLineSegment(sketch, "E15.16.1.3", {"start": v(100.2, -49.07) * mm, "end": v(104.83, -49.07) * mm});
            skLineSegment(sketch, "E15.16.2.0", {"start": v(104.83, -36.37) * mm, "end": v(104.83, -31.75) * mm});
            skLineSegment(sketch, "E15.16.2.1", {"start": v(100.2, -31.75) * mm, "end": v(104.83, -31.75) * mm});
            skLineSegment(sketch, "E15.16.2.2", {"start": v(100.2, -36.37) * mm, "end": v(100.2, -31.75) * mm});
            skLineSegment(sketch, "E15.16.2.3", {"start": v(100.2, -36.37) * mm, "end": v(104.83, -36.37) * mm});
            skLineSegment(sketch, "E15.17.0.0", {"start": v(117.53, -61.77) * mm, "end": v(117.53, -57.15) * mm});
            skLineSegment(sketch, "E15.17.0.1", {"start": v(112.9, -57.15) * mm, "end": v(117.53, -57.15) * mm});
            skLineSegment(sketch, "E15.17.0.2", {"start": v(112.9, -61.77) * mm, "end": v(112.9, -57.15) * mm});
            skLineSegment(sketch, "E15.17.0.3", {"start": v(112.9, -61.77) * mm, "end": v(117.53, -61.77) * mm});
            skLineSegment(sketch, "E15.17.1.0", {"start": v(117.53, -49.07) * mm, "end": v(117.53, -44.45) * mm});
            skLineSegment(sketch, "E15.17.1.1", {"start": v(112.9, -44.45) * mm, "end": v(117.53, -44.45) * mm});
            skLineSegment(sketch, "E15.17.1.2", {"start": v(112.9, -49.07) * mm, "end": v(112.9, -44.45) * mm});
            skLineSegment(sketch, "E15.17.1.3", {"start": v(112.9, -49.07) * mm, "end": v(117.53, -49.07) * mm});
            skLineSegment(sketch, "E15.17.2.0", {"start": v(117.53, -36.37) * mm, "end": v(117.53, -31.75) * mm});
            skLineSegment(sketch, "E15.17.2.1", {"start": v(112.9, -31.75) * mm, "end": v(117.53, -31.75) * mm});
            skLineSegment(sketch, "E15.17.2.2", {"start": v(112.9, -36.37) * mm, "end": v(112.9, -31.75) * mm});
            skLineSegment(sketch, "E15.17.2.3", {"start": v(112.9, -36.37) * mm, "end": v(117.53, -36.37) * mm});
            skLineSegment(sketch, "E15.18.0.0", {"start": v(130.23, -61.77) * mm, "end": v(130.23, -57.15) * mm});
            skLineSegment(sketch, "E15.18.0.1", {"start": v(125.6, -57.15) * mm, "end": v(130.23, -57.15) * mm});
            skLineSegment(sketch, "E15.18.0.2", {"start": v(125.6, -61.77) * mm, "end": v(125.6, -57.15) * mm});
            skLineSegment(sketch, "E15.18.0.3", {"start": v(125.6, -61.77) * mm, "end": v(130.23, -61.77) * mm});
            skLineSegment(sketch, "E15.18.1.0", {"start": v(130.23, -49.07) * mm, "end": v(130.23, -44.45) * mm});
            skLineSegment(sketch, "E15.18.1.1", {"start": v(125.6, -44.45) * mm, "end": v(130.23, -44.45) * mm});
            skLineSegment(sketch, "E15.18.1.2", {"start": v(125.6, -49.07) * mm, "end": v(125.6, -44.45) * mm});
            skLineSegment(sketch, "E15.18.1.3", {"start": v(125.6, -49.07) * mm, "end": v(130.23, -49.07) * mm});
            skLineSegment(sketch, "E15.18.2.0", {"start": v(130.23, -36.37) * mm, "end": v(130.23, -31.75) * mm});
            skLineSegment(sketch, "E15.18.2.1", {"start": v(125.6, -31.75) * mm, "end": v(130.23, -31.75) * mm});
            skLineSegment(sketch, "E15.18.2.2", {"start": v(125.6, -36.37) * mm, "end": v(125.6, -31.75) * mm});
            skLineSegment(sketch, "E15.18.2.3", {"start": v(125.6, -36.37) * mm, "end": v(130.23, -36.37) * mm});
            skLineSegment(sketch, "E15.19.0.0", {"start": v(142.93, -61.77) * mm, "end": v(142.93, -57.15) * mm});
            skLineSegment(sketch, "E15.19.0.1", {"start": v(138.3, -57.15) * mm, "end": v(142.93, -57.15) * mm});
            skLineSegment(sketch, "E15.19.0.2", {"start": v(138.3, -61.77) * mm, "end": v(138.3, -57.15) * mm});
            skLineSegment(sketch, "E15.19.0.3", {"start": v(138.3, -61.77) * mm, "end": v(142.93, -61.77) * mm});
            skLineSegment(sketch, "E15.19.1.0", {"start": v(142.93, -49.07) * mm, "end": v(142.93, -44.45) * mm});
            skLineSegment(sketch, "E15.19.1.1", {"start": v(138.3, -44.45) * mm, "end": v(142.93, -44.45) * mm});
            skLineSegment(sketch, "E15.19.1.2", {"start": v(138.3, -49.07) * mm, "end": v(138.3, -44.45) * mm});
            skLineSegment(sketch, "E15.19.1.3", {"start": v(138.3, -49.07) * mm, "end": v(142.93, -49.07) * mm});
            skLineSegment(sketch, "E15.19.2.0", {"start": v(142.93, -36.37) * mm, "end": v(142.93, -31.75) * mm});
            skLineSegment(sketch, "E15.19.2.1", {"start": v(138.3, -31.75) * mm, "end": v(142.93, -31.75) * mm});
            skLineSegment(sketch, "E15.19.2.2", {"start": v(138.3, -36.37) * mm, "end": v(138.3, -31.75) * mm});
            skLineSegment(sketch, "E15.19.2.3", {"start": v(138.3, -36.37) * mm, "end": v(142.93, -36.37) * mm});
            skLineSegment(sketch, "E15.20.0.0", {"start": v(155.63, -61.77) * mm, "end": v(155.63, -57.15) * mm});
            skLineSegment(sketch, "E15.20.0.1", {"start": v(151, -57.15) * mm, "end": v(155.63, -57.15) * mm});
            skLineSegment(sketch, "E15.20.0.2", {"start": v(151, -61.77) * mm, "end": v(151, -57.15) * mm});
            skLineSegment(sketch, "E15.20.0.3", {"start": v(151, -61.77) * mm, "end": v(155.63, -61.77) * mm});
            skLineSegment(sketch, "E15.20.1.0", {"start": v(155.63, -49.07) * mm, "end": v(155.63, -44.45) * mm});
            skLineSegment(sketch, "E15.20.1.1", {"start": v(151, -44.45) * mm, "end": v(155.63, -44.45) * mm});
            skLineSegment(sketch, "E15.20.1.2", {"start": v(151, -49.07) * mm, "end": v(151, -44.45) * mm});
            skLineSegment(sketch, "E15.20.1.3", {"start": v(151, -49.07) * mm, "end": v(155.63, -49.07) * mm});
            skLineSegment(sketch, "E15.20.2.0", {"start": v(155.63, -36.37) * mm, "end": v(155.63, -31.75) * mm});
            skLineSegment(sketch, "E15.20.2.1", {"start": v(151, -31.75) * mm, "end": v(155.63, -31.75) * mm});
            skLineSegment(sketch, "E15.20.2.2", {"start": v(151, -36.37) * mm, "end": v(151, -31.75) * mm});
            skLineSegment(sketch, "E15.20.2.3", {"start": v(151, -36.37) * mm, "end": v(155.63, -36.37) * mm});
            skLineSegment(sketch, "E15.21.0.0", {"start": v(168.33, -61.77) * mm, "end": v(168.33, -57.15) * mm});
            skLineSegment(sketch, "E15.21.0.1", {"start": v(163.7, -57.15) * mm, "end": v(168.33, -57.15) * mm});
            skLineSegment(sketch, "E15.21.0.2", {"start": v(163.7, -61.77) * mm, "end": v(163.7, -57.15) * mm});
            skLineSegment(sketch, "E15.21.0.3", {"start": v(163.7, -61.77) * mm, "end": v(168.33, -61.77) * mm});
            skLineSegment(sketch, "E15.21.1.0", {"start": v(168.33, -49.07) * mm, "end": v(168.33, -44.45) * mm});
            skLineSegment(sketch, "E15.21.1.1", {"start": v(163.7, -44.45) * mm, "end": v(168.33, -44.45) * mm});
            skLineSegment(sketch, "E15.21.1.2", {"start": v(163.7, -49.07) * mm, "end": v(163.7, -44.45) * mm});
            skLineSegment(sketch, "E15.21.1.3", {"start": v(163.7, -49.07) * mm, "end": v(168.33, -49.07) * mm});
            skLineSegment(sketch, "E15.21.2.0", {"start": v(168.33, -36.37) * mm, "end": v(168.33, -31.75) * mm});
            skLineSegment(sketch, "E15.21.2.1", {"start": v(163.7, -31.75) * mm, "end": v(168.33, -31.75) * mm});
            skLineSegment(sketch, "E15.21.2.2", {"start": v(163.7, -36.37) * mm, "end": v(163.7, -31.75) * mm});
            skLineSegment(sketch, "E15.21.2.3", {"start": v(163.7, -36.37) * mm, "end": v(168.33, -36.37) * mm});
            skLineSegment(sketch, "E15.22.0.0", {"start": v(181.03, -61.77) * mm, "end": v(181.03, -57.15) * mm});
            skLineSegment(sketch, "E15.22.0.1", {"start": v(176.4, -57.15) * mm, "end": v(181.03, -57.15) * mm});
            skLineSegment(sketch, "E15.22.0.2", {"start": v(176.4, -61.77) * mm, "end": v(176.4, -57.15) * mm});
            skLineSegment(sketch, "E15.22.0.3", {"start": v(176.4, -61.77) * mm, "end": v(181.03, -61.77) * mm});
            skLineSegment(sketch, "E15.22.1.0", {"start": v(181.03, -49.07) * mm, "end": v(181.03, -44.45) * mm});
            skLineSegment(sketch, "E15.22.1.1", {"start": v(176.4, -44.45) * mm, "end": v(181.03, -44.45) * mm});
            skLineSegment(sketch, "E15.22.1.2", {"start": v(176.4, -49.07) * mm, "end": v(176.4, -44.45) * mm});
            skLineSegment(sketch, "E15.22.1.3", {"start": v(176.4, -49.07) * mm, "end": v(181.03, -49.07) * mm});
            skLineSegment(sketch, "E15.22.2.0", {"start": v(181.03, -36.37) * mm, "end": v(181.03, -31.75) * mm});
            skLineSegment(sketch, "E15.22.2.1", {"start": v(176.4, -31.75) * mm, "end": v(181.03, -31.75) * mm});
            skLineSegment(sketch, "E15.22.2.2", {"start": v(176.4, -36.37) * mm, "end": v(176.4, -31.75) * mm});
            skLineSegment(sketch, "E15.22.2.3", {"start": v(176.4, -36.37) * mm, "end": v(181.03, -36.37) * mm});
            skLineSegment(sketch, "E15.direction1", {"start": v(-98.37, -61.77) * mm, "end": v(-85.67, -61.77) * mm, "construction": true});
            skLineSegment(sketch, "E15.direction2", {"start": v(-98.37, -61.77) * mm, "end": v(-98.37, -49.07) * mm, "construction": true});
            skLineSegment(sketch, "E16.bottom", {"start": v(54.03, -10.97) * mm, "end": v(49.4, -10.97) * mm});
            skLineSegment(sketch, "E16.top", {"start": v(54.03, -6.35) * mm, "end": v(49.4, -6.35) * mm});
            skLineSegment(sketch, "E16.left", {"start": v(54.03, -10.97) * mm, "end": v(54.03, -6.35) * mm});
            skLineSegment(sketch, "E16.right", {"start": v(49.4, -10.97) * mm, "end": v(49.4, -6.35) * mm});
            skLineSegment(sketch, "E17.bottom", {"start": v(54.03, -19.05) * mm, "end": v(49.4, -19.05) * mm});
            skLineSegment(sketch, "E17.top", {"start": v(54.03, -23.67) * mm, "end": v(49.4, -23.67) * mm});
            skLineSegment(sketch, "E17.left", {"start": v(54.03, -19.05) * mm, "end": v(54.03, -23.67) * mm});
            skLineSegment(sketch, "E17.right", {"start": v(49.4, -19.05) * mm, "end": v(49.4, -23.67) * mm});
            skSolve(sketch);
        }
        {
            var Q0;
            Q0=makeQuery(id+"F10.imprint","IMPRINT",FACE,{"disambiguationData":[TD([[makeQuery(id+"F10.imprint","IMPRINT",EDGE,{"derivedFrom":sQuery(id+"F10.wireOp",EDGE,"E15.0.1.0")}),1.0]])]});
            var Q1;
            Q1=makeQuery(id+"F10.imprint","IMPRINT",FACE,{"disambiguationData":[TD([[makeQuery(id+"F10.imprint","IMPRINT",EDGE,{"derivedFrom":sQuery(id+"F10.wireOp",EDGE,"E15.1.1.0")}),1.0]])]});
            var Q2;
            Q2=makeQuery(id+"F10.imprint","IMPRINT",FACE,{"disambiguationData":[TD([[makeQuery(id+"F10.imprint","IMPRINT",EDGE,{"derivedFrom":sQuery(id+"F10.wireOp",EDGE,"E15.2.0.0")}),1.0]])]});
            var Q3;
            Q3=makeQuery(id+"F10.imprint","IMPRINT",FACE,{"disambiguationData":[TD([[makeQuery(id+"F10.imprint","IMPRINT",EDGE,{"derivedFrom":sQuery(id+"F10.wireOp",EDGE,"E15.2.1.0")}),1.0]])]});
            var Q4;
            Q4=makeQuery(id+"F10.imprint","IMPRINT",FACE,{"disambiguationData":[TD([[makeQuery(id+"F10.imprint","IMPRINT",EDGE,{"derivedFrom":sQuery(id+"F10.wireOp",EDGE,"E15.3.0.0")}),1.0]])]});
            var Q5;
            Q5=makeQuery(id+"F10.imprint","IMPRINT",FACE,{"disambiguationData":[TD([[makeQuery(id+"F10.imprint","IMPRINT",EDGE,{"derivedFrom":sQuery(id+"F10.wireOp",EDGE,"E15.3.1.0")}),1.0]])]});
            var Q6;
            Q6=makeQuery(id+"F10.imprint","IMPRINT",FACE,{"disambiguationData":[TD([[makeQuery(id+"F10.imprint","IMPRINT",EDGE,{"derivedFrom":sQuery(id+"F10.wireOp",EDGE,"E15.4.0.0")}),1.0]])]});
            var Q7;
            Q7=makeQuery(id+"F10.imprint","IMPRINT",FACE,{"disambiguationData":[TD([[makeQuery(id+"F10.imprint","IMPRINT",EDGE,{"derivedFrom":sQuery(id+"F10.wireOp",EDGE,"E15.4.1.0")}),1.0]])]});
            var Q8;
            Q8=makeQuery(id+"F10.imprint","IMPRINT",FACE,{"disambiguationData":[TD([[makeQuery(id+"F10.imprint","IMPRINT",EDGE,{"derivedFrom":sQuery(id+"F10.wireOp",EDGE,"E15.5.0.0")}),1.0]])]});
            var Q9;
            Q9=makeQuery(id+"F10.imprint","IMPRINT",FACE,{"disambiguationData":[TD([[makeQuery(id+"F10.imprint","IMPRINT",EDGE,{"derivedFrom":sQuery(id+"F10.wireOp",EDGE,"E15.5.1.0")}),1.0]])]});
            var Q10;
            Q10=makeQuery(id+"F10.imprint","IMPRINT",FACE,{"disambiguationData":[TD([[makeQuery(id+"F10.imprint","IMPRINT",EDGE,{"derivedFrom":sQuery(id+"F10.wireOp",EDGE,"E15.5.2.0")}),1.0]])]});
            var Q11;
            Q11=makeQuery(id+"F10.imprint","IMPRINT",FACE,{"disambiguationData":[TD([[makeQuery(id+"F10.imprint","IMPRINT",EDGE,{"derivedFrom":sQuery(id+"F10.wireOp",EDGE,"E15.6.0.0")}),1.0]])]});
            var Q12;
            Q12=makeQuery(id+"F10.imprint","IMPRINT",FACE,{"disambiguationData":[TD([[makeQuery(id+"F10.imprint","IMPRINT",EDGE,{"derivedFrom":sQuery(id+"F10.wireOp",EDGE,"E15.6.1.0")}),1.0]])]});
            var Q13;
            Q13=makeQuery(id+"F10.imprint","IMPRINT",FACE,{"disambiguationData":[TD([[makeQuery(id+"F10.imprint","IMPRINT",EDGE,{"derivedFrom":sQuery(id+"F10.wireOp",EDGE,"E15.6.2.0")}),1.0]])]});
            var Q14;
            Q14=makeQuery(id+"F10.imprint","IMPRINT",FACE,{"disambiguationData":[TD([[makeQuery(id+"F10.imprint","IMPRINT",EDGE,{"derivedFrom":sQuery(id+"F10.wireOp",EDGE,"E15.6.3.0")}),1.0]])]});
            var Q15;
            Q15=makeQuery(id+"F10.imprint","IMPRINT",FACE,{"disambiguationData":[TD([[makeQuery(id+"F10.imprint","IMPRINT",EDGE,{"derivedFrom":sQuery(id+"F10.wireOp",EDGE,"E15.7.0.0")}),1.0]])]});
            var Q16;
            Q16=makeQuery(id+"F10.imprint","IMPRINT",FACE,{"disambiguationData":[TD([[makeQuery(id+"F10.imprint","IMPRINT",EDGE,{"derivedFrom":sQuery(id+"F10.wireOp",EDGE,"E15.7.1.0")}),1.0]])]});
            var Q17;
            Q17=makeQuery(id+"F10.imprint","IMPRINT",FACE,{"disambiguationData":[TD([[makeQuery(id+"F10.imprint","IMPRINT",EDGE,{"derivedFrom":sQuery(id+"F10.wireOp",EDGE,"E15.7.2.0")}),1.0]])]});
            var Q18;
            Q18=makeQuery(id+"F10.imprint","IMPRINT",FACE,{"disambiguationData":[TD([[makeQuery(id+"F10.imprint","IMPRINT",EDGE,{"derivedFrom":sQuery(id+"F10.wireOp",EDGE,"E15.7.3.0")}),1.0]])]});
            var Q19;
            Q19=makeQuery(id+"F10.imprint","IMPRINT",FACE,{"disambiguationData":[TD([[makeQuery(id+"F10.imprint","IMPRINT",EDGE,{"derivedFrom":sQuery(id+"F10.wireOp",EDGE,"E15.7.4.0")}),1.0]])]});
            var Q20;
            Q20=makeQuery(id+"F10.imprint","IMPRINT",FACE,{"disambiguationData":[TD([[makeQuery(id+"F10.imprint","IMPRINT",EDGE,{"derivedFrom":sQuery(id+"F10.wireOp",EDGE,"E15.8.0.0")}),1.0]])]});
            var Q21;
            Q21=makeQuery(id+"F10.imprint","IMPRINT",FACE,{"disambiguationData":[TD([[makeQuery(id+"F10.imprint","IMPRINT",EDGE,{"derivedFrom":sQuery(id+"F10.wireOp",EDGE,"E15.8.1.0")}),1.0]])]});
            var Q22;
            Q22=makeQuery(id+"F10.imprint","IMPRINT",FACE,{"disambiguationData":[TD([[makeQuery(id+"F10.imprint","IMPRINT",EDGE,{"derivedFrom":sQuery(id+"F10.wireOp",EDGE,"E15.8.2.0")}),1.0]])]});
            var Q23;
            Q23=makeQuery(id+"F10.imprint","IMPRINT",FACE,{"disambiguationData":[TD([[makeQuery(id+"F10.imprint","IMPRINT",EDGE,{"derivedFrom":sQuery(id+"F10.wireOp",EDGE,"E15.8.3.0")}),1.0]])]});
            var Q24;
            Q24=makeQuery(id+"F10.imprint","IMPRINT",FACE,{"disambiguationData":[TD([[makeQuery(id+"F10.imprint","IMPRINT",EDGE,{"derivedFrom":sQuery(id+"F10.wireOp",EDGE,"E15.8.4.0")}),1.0]])]});
            var Q25;
            Q25=makeQuery(id+"F10.imprint","IMPRINT",FACE,{"disambiguationData":[TD([[makeQuery(id+"F10.imprint","IMPRINT",EDGE,{"derivedFrom":sQuery(id+"F10.wireOp",EDGE,"E15.9.0.0")}),1.0]])]});
            var Q26;
            Q26=makeQuery(id+"F10.imprint","IMPRINT",FACE,{"disambiguationData":[TD([[makeQuery(id+"F10.imprint","IMPRINT",EDGE,{"derivedFrom":sQuery(id+"F10.wireOp",EDGE,"E15.9.1.0")}),1.0]])]});
            var Q27;
            Q27=makeQuery(id+"F10.imprint","IMPRINT",FACE,{"disambiguationData":[TD([[makeQuery(id+"F10.imprint","IMPRINT",EDGE,{"derivedFrom":sQuery(id+"F10.wireOp",EDGE,"E15.9.2.0")}),1.0]])]});
            var Q28;
            Q28=makeQuery(id+"F10.imprint","IMPRINT",FACE,{"disambiguationData":[TD([[makeQuery(id+"F10.imprint","IMPRINT",EDGE,{"derivedFrom":sQuery(id+"F10.wireOp",EDGE,"E15.9.3.0")}),1.0]])]});
            var Q29;
            Q29=makeQuery(id+"F10.imprint","IMPRINT",FACE,{"disambiguationData":[TD([[makeQuery(id+"F10.imprint","IMPRINT",EDGE,{"derivedFrom":sQuery(id+"F10.wireOp",EDGE,"E15.9.4.0")}),1.0]])]});
            var Q30;
            Q30=makeQuery(id+"F10.imprint","IMPRINT",FACE,{"disambiguationData":[TD([[makeQuery(id+"F10.imprint","IMPRINT",EDGE,{"derivedFrom":sQuery(id+"F10.wireOp",EDGE,"E15.10.0.0")}),1.0]])]});
            var Q31;
            Q31=makeQuery(id+"F10.imprint","IMPRINT",FACE,{"disambiguationData":[TD([[makeQuery(id+"F10.imprint","IMPRINT",EDGE,{"derivedFrom":sQuery(id+"F10.wireOp",EDGE,"E15.10.1.0")}),1.0]])]});
            var Q32;
            Q32=makeQuery(id+"F10.imprint","IMPRINT",FACE,{"disambiguationData":[TD([[makeQuery(id+"F10.imprint","IMPRINT",EDGE,{"derivedFrom":sQuery(id+"F10.wireOp",EDGE,"E15.10.2.0")}),1.0]])]});
            var Q33;
            Q33=makeQuery(id+"F10.imprint","IMPRINT",FACE,{"disambiguationData":[TD([[makeQuery(id+"F10.imprint","IMPRINT",EDGE,{"derivedFrom":sQuery(id+"F10.wireOp",EDGE,"E15.10.3.0")}),1.0]])]});
            var Q34;
            Q34=makeQuery(id+"F10.imprint","IMPRINT",FACE,{"disambiguationData":[TD([[makeQuery(id+"F10.imprint","IMPRINT",EDGE,{"derivedFrom":sQuery(id+"F10.wireOp",EDGE,"E15.10.4.0")}),1.0]])]});
            var Q35;
            Q35=makeQuery(id+"F10.imprint","IMPRINT",FACE,{"disambiguationData":[TD([[makeQuery(id+"F10.imprint","IMPRINT",EDGE,{"derivedFrom":sQuery(id+"F10.wireOp",EDGE,"E15.11.0.0")}),1.0]])]});
            var Q36;
            Q36=makeQuery(id+"F10.imprint","IMPRINT",FACE,{"disambiguationData":[TD([[makeQuery(id+"F10.imprint","IMPRINT",EDGE,{"derivedFrom":sQuery(id+"F10.wireOp",EDGE,"E15.11.1.0")}),1.0]])]});
            var Q37;
            Q37=makeQuery(id+"F10.imprint","IMPRINT",FACE,{"disambiguationData":[TD([[makeQuery(id+"F10.imprint","IMPRINT",EDGE,{"derivedFrom":sQuery(id+"F10.wireOp",EDGE,"E15.11.2.0")}),1.0]])]});
            var Q38;
            Q38=makeQuery(id+"F10.imprint","IMPRINT",FACE,{"disambiguationData":[TD([[makeQuery(id+"F10.imprint","IMPRINT",EDGE,{"derivedFrom":sQuery(id+"F10.wireOp",EDGE,"E15.11.3.0")}),1.0]])]});
            var Q39;
            Q39=makeQuery(id+"F10.imprint","IMPRINT",FACE,{"disambiguationData":[TD([[makeQuery(id+"F10.imprint","IMPRINT",EDGE,{"derivedFrom":sQuery(id+"F10.wireOp",EDGE,"E15.11.4.0")}),1.0]])]});
            var Q40;
            Q40=makeQuery(id+"F10.imprint","IMPRINT",FACE,{"disambiguationData":[TD([[makeQuery(id+"F10.imprint","IMPRINT",EDGE,{"derivedFrom":sQuery(id+"F10.wireOp",EDGE,"E15.12.0.0")}),1.0]])]});
            var Q41;
            Q41=makeQuery(id+"F10.imprint","IMPRINT",FACE,{"disambiguationData":[TD([[makeQuery(id+"F10.imprint","IMPRINT",EDGE,{"derivedFrom":sQuery(id+"F10.wireOp",EDGE,"E15.12.1.0")}),1.0]])]});
            var Q42;
            Q42=makeQuery(id+"F10.imprint","IMPRINT",FACE,{"disambiguationData":[TD([[makeQuery(id+"F10.imprint","IMPRINT",EDGE,{"derivedFrom":sQuery(id+"F10.wireOp",EDGE,"E15.12.2.0")}),1.0]])]});
            var Q43;
            Q43=makeQuery(id+"F10.imprint","IMPRINT",FACE,{"disambiguationData":[TD([[makeQuery(id+"F10.imprint","IMPRINT",EDGE,{"derivedFrom":sQuery(id+"F10.wireOp",EDGE,"E15.13.0.0")}),1.0]])]});
            var Q44;
            Q44=makeQuery(id+"F10.imprint","IMPRINT",FACE,{"disambiguationData":[TD([[makeQuery(id+"F10.imprint","IMPRINT",EDGE,{"derivedFrom":sQuery(id+"F10.wireOp",EDGE,"E15.13.1.0")}),1.0]])]});
            var Q45;
            Q45=makeQuery(id+"F10.imprint","IMPRINT",FACE,{"disambiguationData":[TD([[makeQuery(id+"F10.imprint","IMPRINT",EDGE,{"derivedFrom":sQuery(id+"F10.wireOp",EDGE,"E15.13.2.0")}),1.0]])]});
            var Q46;
            Q46=makeQuery(id+"F10.imprint","IMPRINT",FACE,{"disambiguationData":[TD([[makeQuery(id+"F10.imprint","IMPRINT",EDGE,{"derivedFrom":sQuery(id+"F10.wireOp",EDGE,"E15.14.0.0")}),1.0]])]});
            var Q47;
            Q47=makeQuery(id+"F10.imprint","IMPRINT",FACE,{"disambiguationData":[TD([[makeQuery(id+"F10.imprint","IMPRINT",EDGE,{"derivedFrom":sQuery(id+"F10.wireOp",EDGE,"E15.14.1.0")}),1.0]])]});
            var Q48;
            Q48=makeQuery(id+"F10.imprint","IMPRINT",FACE,{"disambiguationData":[TD([[makeQuery(id+"F10.imprint","IMPRINT",EDGE,{"derivedFrom":sQuery(id+"F10.wireOp",EDGE,"E15.14.2.0")}),1.0]])]});
            var Q49;
            Q49=makeQuery(id+"F10.imprint","IMPRINT",FACE,{"disambiguationData":[TD([[makeQuery(id+"F10.imprint","IMPRINT",EDGE,{"derivedFrom":sQuery(id+"F10.wireOp",EDGE,"E15.15.0.0")}),1.0]])]});
            var Q50;
            Q50=makeQuery(id+"F10.imprint","IMPRINT",FACE,{"disambiguationData":[TD([[makeQuery(id+"F10.imprint","IMPRINT",EDGE,{"derivedFrom":sQuery(id+"F10.wireOp",EDGE,"E15.15.1.0")}),1.0]])]});
            var Q51;
            Q51=makeQuery(id+"F10.imprint","IMPRINT",FACE,{"disambiguationData":[TD([[makeQuery(id+"F10.imprint","IMPRINT",EDGE,{"derivedFrom":sQuery(id+"F10.wireOp",EDGE,"E15.15.2.0")}),1.0]])]});
            var Q52;
            Q52=makeQuery(id+"F10.imprint","IMPRINT",FACE,{"disambiguationData":[TD([[makeQuery(id+"F10.imprint","IMPRINT",EDGE,{"derivedFrom":sQuery(id+"F10.wireOp",EDGE,"E15.16.0.0")}),1.0]])]});
            var Q53;
            Q53=makeQuery(id+"F10.imprint","IMPRINT",FACE,{"disambiguationData":[TD([[makeQuery(id+"F10.imprint","IMPRINT",EDGE,{"derivedFrom":sQuery(id+"F10.wireOp",EDGE,"E15.16.1.0")}),1.0]])]});
            var Q54;
            Q54=makeQuery(id+"F10.imprint","IMPRINT",FACE,{"disambiguationData":[TD([[makeQuery(id+"F10.imprint","IMPRINT",EDGE,{"derivedFrom":sQuery(id+"F10.wireOp",EDGE,"E15.16.2.0")}),1.0]])]});
            var Q55;
            Q55=makeQuery(id+"F10.imprint","IMPRINT",FACE,{"disambiguationData":[TD([[makeQuery(id+"F10.imprint","IMPRINT",EDGE,{"derivedFrom":sQuery(id+"F10.wireOp",EDGE,"E15.17.0.0")}),1.0]])]});
            var Q56;
            Q56=makeQuery(id+"F10.imprint","IMPRINT",FACE,{"disambiguationData":[TD([[makeQuery(id+"F10.imprint","IMPRINT",EDGE,{"derivedFrom":sQuery(id+"F10.wireOp",EDGE,"E15.17.1.0")}),1.0]])]});
            var Q57;
            Q57=makeQuery(id+"F10.imprint","IMPRINT",FACE,{"disambiguationData":[TD([[makeQuery(id+"F10.imprint","IMPRINT",EDGE,{"derivedFrom":sQuery(id+"F10.wireOp",EDGE,"E15.17.2.0")}),1.0]])]});
            var Q58;
            Q58=makeQuery(id+"F10.imprint","IMPRINT",FACE,{"disambiguationData":[TD([[makeQuery(id+"F10.imprint","IMPRINT",EDGE,{"derivedFrom":sQuery(id+"F10.wireOp",EDGE,"E15.18.0.0")}),1.0]])]});
            var Q59;
            Q59=makeQuery(id+"F10.imprint","IMPRINT",FACE,{"disambiguationData":[TD([[makeQuery(id+"F10.imprint","IMPRINT",EDGE,{"derivedFrom":sQuery(id+"F10.wireOp",EDGE,"E15.18.1.0")}),1.0]])]});
            var Q60;
            Q60=makeQuery(id+"F10.imprint","IMPRINT",FACE,{"disambiguationData":[TD([[makeQuery(id+"F10.imprint","IMPRINT",EDGE,{"derivedFrom":sQuery(id+"F10.wireOp",EDGE,"E15.18.2.0")}),1.0]])]});
            var Q61;
            Q61=makeQuery(id+"F10.imprint","IMPRINT",FACE,{"disambiguationData":[TD([[makeQuery(id+"F10.imprint","IMPRINT",EDGE,{"derivedFrom":sQuery(id+"F10.wireOp",EDGE,"E15.19.0.0")}),1.0]])]});
            var Q62;
            Q62=makeQuery(id+"F10.imprint","IMPRINT",FACE,{"disambiguationData":[TD([[makeQuery(id+"F10.imprint","IMPRINT",EDGE,{"derivedFrom":sQuery(id+"F10.wireOp",EDGE,"E15.19.1.0")}),1.0]])]});
            var Q63;
            Q63=makeQuery(id+"F10.imprint","IMPRINT",FACE,{"disambiguationData":[TD([[makeQuery(id+"F10.imprint","IMPRINT",EDGE,{"derivedFrom":sQuery(id+"F10.wireOp",EDGE,"E15.19.2.0")}),1.0]])]});
            var Q64;
            Q64=makeQuery(id+"F10.imprint","IMPRINT",FACE,{"disambiguationData":[TD([[makeQuery(id+"F10.imprint","IMPRINT",EDGE,{"derivedFrom":sQuery(id+"F10.wireOp",EDGE,"E15.20.0.0")}),1.0]])]});
            var Q65;
            Q65=makeQuery(id+"F10.imprint","IMPRINT",FACE,{"disambiguationData":[TD([[makeQuery(id+"F10.imprint","IMPRINT",EDGE,{"derivedFrom":sQuery(id+"F10.wireOp",EDGE,"E15.20.1.0")}),1.0]])]});
            var Q66;
            Q66=makeQuery(id+"F10.imprint","IMPRINT",FACE,{"disambiguationData":[TD([[makeQuery(id+"F10.imprint","IMPRINT",EDGE,{"derivedFrom":sQuery(id+"F10.wireOp",EDGE,"E15.20.2.0")}),1.0]])]});
            var Q67;
            Q67=makeQuery(id+"F10.imprint","IMPRINT",FACE,{"disambiguationData":[TD([[makeQuery(id+"F10.imprint","IMPRINT",EDGE,{"derivedFrom":sQuery(id+"F10.wireOp",EDGE,"E15.21.0.0")}),1.0]])]});
            var Q68;
            Q68=makeQuery(id+"F10.imprint","IMPRINT",FACE,{"disambiguationData":[TD([[makeQuery(id+"F10.imprint","IMPRINT",EDGE,{"derivedFrom":sQuery(id+"F10.wireOp",EDGE,"E15.21.1.0")}),1.0]])]});
            var Q69;
            Q69=makeQuery(id+"F10.imprint","IMPRINT",FACE,{"disambiguationData":[TD([[makeQuery(id+"F10.imprint","IMPRINT",EDGE,{"derivedFrom":sQuery(id+"F10.wireOp",EDGE,"E15.21.2.0")}),1.0]])]});
            var Q70;
            Q70=makeQuery(id+"F10.imprint","IMPRINT",FACE,{"disambiguationData":[TD([[makeQuery(id+"F10.imprint","IMPRINT",EDGE,{"derivedFrom":sQuery(id+"F10.wireOp",EDGE,"E15.22.0.0")}),1.0]])]});
            var Q71;
            Q71=makeQuery(id+"F10.imprint","IMPRINT",FACE,{"disambiguationData":[TD([[makeQuery(id+"F10.imprint","IMPRINT",EDGE,{"derivedFrom":sQuery(id+"F10.wireOp",EDGE,"E15.22.1.0")}),1.0]])]});
            var Q72;
            Q72=makeQuery(id+"F10.imprint","IMPRINT",FACE,{"disambiguationData":[TD([[makeQuery(id+"F10.imprint","IMPRINT",EDGE,{"derivedFrom":sQuery(id+"F10.wireOp",EDGE,"E15.22.2.0")}),1.0]])]});
            var Q73;
            Q73=makeQuery(id+"F10.imprint","IMPRINT",FACE,{"disambiguationData":[TD([[makeQuery(id+"F10.imprint","IMPRINT",EDGE,{"derivedFrom":sQuery(id+"F10.wireOp",EDGE,"E15.1.0.0")}),1.0]])]});
            var Q74;
            Q74=makeQuery(id+"F10.imprint","IMPRINT",FACE,{"disambiguationData":[TD([[makeQuery(id+"F10.imprint","IMPRINT",EDGE,{"derivedFrom":sQuery(id+"F10.wireOp",EDGE,"E14.bottom")}),1.0]])]});
            var Q75;
            Q75=makeQuery(id+"F10.imprint","IMPRINT",FACE,{"disambiguationData":[TD([[makeQuery(id+"F10.imprint","IMPRINT",EDGE,{"derivedFrom":sQuery(id+"F10.wireOp",EDGE,"E16.bottom")}),-1.0]])]});
            var Q76;
            Q76=makeQuery(id+"F10.imprint","IMPRINT",FACE,{"disambiguationData":[TD([[makeQuery(id+"F10.imprint","IMPRINT",EDGE,{"derivedFrom":sQuery(id+"F10.wireOp",EDGE,"E17.bottom")}),1.0]])]});
            extrude(context, id + "F11", {"entities" : qUnion([Q0, Q1, Q2, Q3, Q4, Q5, Q6, Q7, Q8, Q9, Q10, Q11, Q12, Q13, Q14, Q15, Q16, Q17, Q18, Q19, Q20, Q21, Q22, Q23, Q24, Q25, Q26, Q27, Q28, Q29, Q30, Q31, Q32, Q33, Q34, Q35, Q36, Q37, Q38, Q39, Q40, Q41, Q42, Q43, Q44, Q45, Q46, Q47, Q48, Q49, Q50, Q51, Q52, Q53, Q54, Q55, Q56, Q57, Q58, Q59, Q60, Q61, Q62, Q63, Q64, Q65, Q66, Q67, Q68, Q69, Q70, Q71, Q72, Q73, Q74, Q75, Q76]), "operationType" : NewBodyOperationType.REMOVE, "endBound" : BoundingType.THROUGH_ALL, "oppositeDirection" : true, "depth" : 25.4 * mm});
        }
        {
            var Q0;
            Q0=makeQuery(id+"F3.boolean.opBoolean","COPY",FACE,{"derivedFrom":makeQuery(id+"F3.opExtrude","SWEPT_FACE",FACE,{"disambiguationData":[OSD([sQuery(id+"F2.wireOp",EDGE,"E2")])]})});
            var sketch = newSketch(context, id + "F12", { "sketchPlane" : qUnion([Q0])});
            skLineSegment(sketch, "E18", {"start": v(-45.03, -14.28) * mm, "end": v(-45.03, -65.08) * mm});
            skLineSegment(sketch, "E19", {"start": v(69.27, -14.28) * mm, "end": v(69.27, -65.08) * mm});
            skSolve(sketch);
        }
        {
            var Q0;
            Q0=makeQuery(id+"F9.boolean.opBoolean","COPY",FACE,{"derivedFrom":makeQuery(id+"F9.opExtrude","SWEPT_FACE",FACE,{"disambiguationData":[OSD([sQuery(id+"F2.wireOp",EDGE,"E1"),sQuery(id+"F2.wireOp",EDGE,"E2")])]})});
            var sketch = newSketch(context, id + "F13", { "sketchPlane" : qUnion([Q0])});
            skLineSegment(sketch, "E20", {"start": v(-45.04, -38.1) * mm, "end": v(-45.04, -63.5) * mm});
            skLineSegment(sketch, "E21", {"start": v(69.04, -38.1) * mm, "end": v(69.04, -63.5) * mm});
            skSolve(sketch);
        }
        {
            var Q0;
            {var subQ0=sQuery(id+"F13.wireOp",EDGE,"E20");Q0=makeQuery(id+"F13.imprint","IMPRINT",FACE,{"disambiguationData":[TD([[makeQuery(id+"F13.imprint","IMPRINT",EDGE,{"derivedFrom":subQ0}),1.0]])]});}
            var Q1;
            {var subQ0=sQuery(id+"F12.wireOp",EDGE,"E18");Q1=makeQuery(id+"F12.imprint","IMPRINT",FACE,{"disambiguationData":[TD([[makeQuery(id+"F12.imprint","IMPRINT",EDGE,{"derivedFrom":subQ0}),1.0]])]});}
            var Q2;
            Q2=makeQuery(id+"F7.boolean.opBoolean","COPY",FACE,{"derivedFrom":makeQuery(id+"F7.opExtrude","SWEPT_FACE",FACE,{"disambiguationData":[OSD([sQuery(id+"F6.wireOp",EDGE,"E8.top")])]})});
            extrude(context, id + "F14", {"entities" : qUnion([Q0, Q1]), "operationType" : NewBodyOperationType.REMOVE, "endBound" : BoundingType.UP_TO_SURFACE, "oppositeDirection" : true, "endBoundEntityFace" : qUnion([Q2]), "depth" : 25.4 * mm});
        }
        {
            var Q0;
            Q0=makeQuery(id+"F1.opExtrude","SWEPT_FACE",FACE,{"disambiguationData":[OSD([sQuery(id+"F0.wireOp",EDGE,"E0.bottom")])]});
            var sketch = newSketch(context, id + "F15", { "sketchPlane" : qUnion([Q0])});
            skLineSegment(sketch, "E22", {"start": v(-81.97, -25.4) * mm, "end": v(-72.44, -25.4) * mm});
            skLineSegment(sketch, "E23", {"start": v(-72.44, -25.4) * mm, "end": v(-72.44, -63.5) * mm});
            skLineSegment(sketch, "E24", {"start": v(57.73, -25.4) * mm, "end": v(48.2, -25.4) * mm});
            skLineSegment(sketch, "E25", {"start": v(48.2, -25.4) * mm, "end": v(48.2, -63.5) * mm});
            skLineSegment(sketch, "E26", {"start": v(48.2, -63.5) * mm, "end": v(-72.44, -63.5) * mm});
            skLineSegment(sketch, "E27.bottom", {"start": v(-72.44, -63.5) * mm, "end": v(-64.37, -63.5) * mm});
            skLineSegment(sketch, "E27.top", {"start": v(-72.44, -58.88) * mm, "end": v(-64.37, -58.88) * mm});
            skLineSegment(sketch, "E27.left", {"start": v(-72.44, -63.5) * mm, "end": v(-72.44, -58.88) * mm});
            skLineSegment(sketch, "E27.right", {"start": v(-64.37, -63.5) * mm, "end": v(-64.37, -58.88) * mm});
            skLineSegment(sketch, "E28.bottom", {"start": v(-64.37, -58.88) * mm, "end": v(-59.74, -58.88) * mm});
            skLineSegment(sketch, "E28.top", {"start": v(-64.37, -54.25) * mm, "end": v(-59.74, -54.25) * mm});
            skLineSegment(sketch, "E28.left", {"start": v(-64.37, -58.88) * mm, "end": v(-64.37, -54.25) * mm});
            skLineSegment(sketch, "E28.right", {"start": v(-59.74, -58.88) * mm, "end": v(-59.74, -54.25) * mm});
            skLineSegment(sketch, "E29.0.1.0", {"start": v(-64.37, -46.18) * mm, "end": v(-64.37, -41.55) * mm});
            skLineSegment(sketch, "E29.0.1.1", {"start": v(-64.37, -41.55) * mm, "end": v(-59.74, -41.55) * mm});
            skLineSegment(sketch, "E29.0.1.2", {"start": v(-59.74, -46.18) * mm, "end": v(-59.74, -41.55) * mm});
            skLineSegment(sketch, "E29.0.1.3", {"start": v(-64.37, -46.18) * mm, "end": v(-59.74, -46.18) * mm});
            skLineSegment(sketch, "E29.0.2.0", {"start": v(-64.37, -33.48) * mm, "end": v(-64.37, -28.85) * mm});
            skLineSegment(sketch, "E29.0.2.1", {"start": v(-64.37, -28.85) * mm, "end": v(-59.74, -28.85) * mm});
            skLineSegment(sketch, "E29.0.2.2", {"start": v(-59.74, -33.48) * mm, "end": v(-59.74, -28.85) * mm});
            skLineSegment(sketch, "E29.0.2.3", {"start": v(-64.37, -33.48) * mm, "end": v(-59.74, -33.48) * mm});
            skLineSegment(sketch, "E29.1.0.0", {"start": v(-51.67, -58.88) * mm, "end": v(-51.67, -54.25) * mm});
            skLineSegment(sketch, "E29.1.0.1", {"start": v(-51.67, -54.25) * mm, "end": v(-47.04, -54.25) * mm});
            skLineSegment(sketch, "E29.1.0.2", {"start": v(-47.04, -58.88) * mm, "end": v(-47.04, -54.25) * mm});
            skLineSegment(sketch, "E29.1.0.3", {"start": v(-51.67, -58.88) * mm, "end": v(-47.04, -58.88) * mm});
            skLineSegment(sketch, "E29.1.1.0", {"start": v(-51.67, -46.18) * mm, "end": v(-51.67, -41.55) * mm});
            skLineSegment(sketch, "E29.1.1.1", {"start": v(-51.67, -41.55) * mm, "end": v(-47.04, -41.55) * mm});
            skLineSegment(sketch, "E29.1.1.2", {"start": v(-47.04, -46.18) * mm, "end": v(-47.04, -41.55) * mm});
            skLineSegment(sketch, "E29.1.1.3", {"start": v(-51.67, -46.18) * mm, "end": v(-47.04, -46.18) * mm});
            skLineSegment(sketch, "E29.1.2.0", {"start": v(-51.67, -33.48) * mm, "end": v(-51.67, -28.85) * mm});
            skLineSegment(sketch, "E29.1.2.1", {"start": v(-51.67, -28.85) * mm, "end": v(-47.04, -28.85) * mm});
            skLineSegment(sketch, "E29.1.2.2", {"start": v(-47.04, -33.48) * mm, "end": v(-47.04, -28.85) * mm});
            skLineSegment(sketch, "E29.1.2.3", {"start": v(-51.67, -33.48) * mm, "end": v(-47.04, -33.48) * mm});
            skLineSegment(sketch, "E29.2.0.0", {"start": v(-38.97, -58.88) * mm, "end": v(-38.97, -54.25) * mm});
            skLineSegment(sketch, "E29.2.0.1", {"start": v(-38.97, -54.25) * mm, "end": v(-34.34, -54.25) * mm});
            skLineSegment(sketch, "E29.2.0.2", {"start": v(-34.34, -58.88) * mm, "end": v(-34.34, -54.25) * mm});
            skLineSegment(sketch, "E29.2.0.3", {"start": v(-38.97, -58.88) * mm, "end": v(-34.34, -58.88) * mm});
            skLineSegment(sketch, "E29.2.1.0", {"start": v(-38.97, -46.18) * mm, "end": v(-38.97, -41.55) * mm});
            skLineSegment(sketch, "E29.2.1.1", {"start": v(-38.97, -41.55) * mm, "end": v(-34.34, -41.55) * mm});
            skLineSegment(sketch, "E29.2.1.2", {"start": v(-34.34, -46.18) * mm, "end": v(-34.34, -41.55) * mm});
            skLineSegment(sketch, "E29.2.1.3", {"start": v(-38.97, -46.18) * mm, "end": v(-34.34, -46.18) * mm});
            skLineSegment(sketch, "E29.2.2.0", {"start": v(-38.97, -33.48) * mm, "end": v(-38.97, -28.85) * mm});
            skLineSegment(sketch, "E29.2.2.1", {"start": v(-38.97, -28.85) * mm, "end": v(-34.34, -28.85) * mm});
            skLineSegment(sketch, "E29.2.2.2", {"start": v(-34.34, -33.48) * mm, "end": v(-34.34, -28.85) * mm});
            skLineSegment(sketch, "E29.2.2.3", {"start": v(-38.97, -33.48) * mm, "end": v(-34.34, -33.48) * mm});
            skLineSegment(sketch, "E29.3.0.0", {"start": v(-26.27, -58.88) * mm, "end": v(-26.27, -54.25) * mm});
            skLineSegment(sketch, "E29.3.0.1", {"start": v(-26.27, -54.25) * mm, "end": v(-21.64, -54.25) * mm});
            skLineSegment(sketch, "E29.3.0.2", {"start": v(-21.64, -58.88) * mm, "end": v(-21.64, -54.25) * mm});
            skLineSegment(sketch, "E29.3.0.3", {"start": v(-26.27, -58.88) * mm, "end": v(-21.64, -58.88) * mm});
            skLineSegment(sketch, "E29.3.1.0", {"start": v(-26.27, -46.18) * mm, "end": v(-26.27, -41.55) * mm});
            skLineSegment(sketch, "E29.3.1.1", {"start": v(-26.27, -41.55) * mm, "end": v(-21.64, -41.55) * mm});
            skLineSegment(sketch, "E29.3.1.2", {"start": v(-21.64, -46.18) * mm, "end": v(-21.64, -41.55) * mm});
            skLineSegment(sketch, "E29.3.1.3", {"start": v(-26.27, -46.18) * mm, "end": v(-21.64, -46.18) * mm});
            skLineSegment(sketch, "E29.3.2.0", {"start": v(-26.27, -33.48) * mm, "end": v(-26.27, -28.85) * mm});
            skLineSegment(sketch, "E29.3.2.1", {"start": v(-26.27, -28.85) * mm, "end": v(-21.64, -28.85) * mm});
            skLineSegment(sketch, "E29.3.2.2", {"start": v(-21.64, -33.48) * mm, "end": v(-21.64, -28.85) * mm});
            skLineSegment(sketch, "E29.3.2.3", {"start": v(-26.27, -33.48) * mm, "end": v(-21.64, -33.48) * mm});
            skLineSegment(sketch, "E29.4.0.0", {"start": v(-13.57, -58.88) * mm, "end": v(-13.57, -54.25) * mm});
            skLineSegment(sketch, "E29.4.0.1", {"start": v(-13.57, -54.25) * mm, "end": v(-8.94, -54.25) * mm});
            skLineSegment(sketch, "E29.4.0.2", {"start": v(-8.94, -58.88) * mm, "end": v(-8.94, -54.25) * mm});
            skLineSegment(sketch, "E29.4.0.3", {"start": v(-13.57, -58.88) * mm, "end": v(-8.94, -58.88) * mm});
            skLineSegment(sketch, "E29.4.1.0", {"start": v(-13.57, -46.18) * mm, "end": v(-13.57, -41.55) * mm});
            skLineSegment(sketch, "E29.4.1.1", {"start": v(-13.57, -41.55) * mm, "end": v(-8.94, -41.55) * mm});
            skLineSegment(sketch, "E29.4.1.2", {"start": v(-8.94, -46.18) * mm, "end": v(-8.94, -41.55) * mm});
            skLineSegment(sketch, "E29.4.1.3", {"start": v(-13.57, -46.18) * mm, "end": v(-8.94, -46.18) * mm});
            skLineSegment(sketch, "E29.4.2.0", {"start": v(-13.57, -33.48) * mm, "end": v(-13.57, -28.85) * mm});
            skLineSegment(sketch, "E29.4.2.1", {"start": v(-13.57, -28.85) * mm, "end": v(-8.94, -28.85) * mm});
            skLineSegment(sketch, "E29.4.2.2", {"start": v(-8.94, -33.48) * mm, "end": v(-8.94, -28.85) * mm});
            skLineSegment(sketch, "E29.4.2.3", {"start": v(-13.57, -33.48) * mm, "end": v(-8.94, -33.48) * mm});
            skLineSegment(sketch, "E29.5.0.0", {"start": v(-0.87, -58.88) * mm, "end": v(-0.87, -54.25) * mm});
            skLineSegment(sketch, "E29.5.0.1", {"start": v(-0.87, -54.25) * mm, "end": v(3.76, -54.25) * mm});
            skLineSegment(sketch, "E29.5.0.2", {"start": v(3.76, -58.88) * mm, "end": v(3.76, -54.25) * mm});
            skLineSegment(sketch, "E29.5.0.3", {"start": v(-0.87, -58.88) * mm, "end": v(3.76, -58.88) * mm});
            skLineSegment(sketch, "E29.5.1.0", {"start": v(-0.87, -46.18) * mm, "end": v(-0.87, -41.55) * mm});
            skLineSegment(sketch, "E29.5.1.1", {"start": v(-0.87, -41.55) * mm, "end": v(3.76, -41.55) * mm});
            skLineSegment(sketch, "E29.5.1.2", {"start": v(3.76, -46.18) * mm, "end": v(3.76, -41.55) * mm});
            skLineSegment(sketch, "E29.5.1.3", {"start": v(-0.87, -46.18) * mm, "end": v(3.76, -46.18) * mm});
            skLineSegment(sketch, "E29.5.2.0", {"start": v(-0.87, -33.48) * mm, "end": v(-0.87, -28.85) * mm});
            skLineSegment(sketch, "E29.5.2.1", {"start": v(-0.87, -28.85) * mm, "end": v(3.76, -28.85) * mm});
            skLineSegment(sketch, "E29.5.2.2", {"start": v(3.76, -33.48) * mm, "end": v(3.76, -28.85) * mm});
            skLineSegment(sketch, "E29.5.2.3", {"start": v(-0.87, -33.48) * mm, "end": v(3.76, -33.48) * mm});
            skLineSegment(sketch, "E29.6.0.0", {"start": v(11.83, -58.88) * mm, "end": v(11.83, -54.25) * mm});
            skLineSegment(sketch, "E29.6.0.1", {"start": v(11.83, -54.25) * mm, "end": v(16.46, -54.25) * mm});
            skLineSegment(sketch, "E29.6.0.2", {"start": v(16.46, -58.88) * mm, "end": v(16.46, -54.25) * mm});
            skLineSegment(sketch, "E29.6.0.3", {"start": v(11.83, -58.88) * mm, "end": v(16.46, -58.88) * mm});
            skLineSegment(sketch, "E29.6.1.0", {"start": v(11.83, -46.18) * mm, "end": v(11.83, -41.55) * mm});
            skLineSegment(sketch, "E29.6.1.1", {"start": v(11.83, -41.55) * mm, "end": v(16.46, -41.55) * mm});
            skLineSegment(sketch, "E29.6.1.2", {"start": v(16.46, -46.18) * mm, "end": v(16.46, -41.55) * mm});
            skLineSegment(sketch, "E29.6.1.3", {"start": v(11.83, -46.18) * mm, "end": v(16.46, -46.18) * mm});
            skLineSegment(sketch, "E29.6.2.0", {"start": v(11.83, -33.48) * mm, "end": v(11.83, -28.85) * mm});
            skLineSegment(sketch, "E29.6.2.1", {"start": v(11.83, -28.85) * mm, "end": v(16.46, -28.85) * mm});
            skLineSegment(sketch, "E29.6.2.2", {"start": v(16.46, -33.48) * mm, "end": v(16.46, -28.85) * mm});
            skLineSegment(sketch, "E29.6.2.3", {"start": v(11.83, -33.48) * mm, "end": v(16.46, -33.48) * mm});
            skLineSegment(sketch, "E29.7.0.0", {"start": v(24.53, -58.88) * mm, "end": v(24.53, -54.25) * mm});
            skLineSegment(sketch, "E29.7.0.1", {"start": v(24.53, -54.25) * mm, "end": v(29.16, -54.25) * mm});
            skLineSegment(sketch, "E29.7.0.2", {"start": v(29.16, -58.88) * mm, "end": v(29.16, -54.25) * mm});
            skLineSegment(sketch, "E29.7.0.3", {"start": v(24.53, -58.88) * mm, "end": v(29.16, -58.88) * mm});
            skLineSegment(sketch, "E29.7.1.0", {"start": v(24.53, -46.18) * mm, "end": v(24.53, -41.55) * mm});
            skLineSegment(sketch, "E29.7.1.1", {"start": v(24.53, -41.55) * mm, "end": v(29.16, -41.55) * mm});
            skLineSegment(sketch, "E29.7.1.2", {"start": v(29.16, -46.18) * mm, "end": v(29.16, -41.55) * mm});
            skLineSegment(sketch, "E29.7.1.3", {"start": v(24.53, -46.18) * mm, "end": v(29.16, -46.18) * mm});
            skLineSegment(sketch, "E29.7.2.0", {"start": v(24.53, -33.48) * mm, "end": v(24.53, -28.85) * mm});
            skLineSegment(sketch, "E29.7.2.1", {"start": v(24.53, -28.85) * mm, "end": v(29.16, -28.85) * mm});
            skLineSegment(sketch, "E29.7.2.2", {"start": v(29.16, -33.48) * mm, "end": v(29.16, -28.85) * mm});
            skLineSegment(sketch, "E29.7.2.3", {"start": v(24.53, -33.48) * mm, "end": v(29.16, -33.48) * mm});
            skLineSegment(sketch, "E29.8.0.0", {"start": v(37.23, -58.88) * mm, "end": v(37.23, -54.25) * mm});
            skLineSegment(sketch, "E29.8.0.1", {"start": v(37.23, -54.25) * mm, "end": v(41.86, -54.25) * mm});
            skLineSegment(sketch, "E29.8.0.2", {"start": v(41.86, -58.88) * mm, "end": v(41.86, -54.25) * mm});
            skLineSegment(sketch, "E29.8.0.3", {"start": v(37.23, -58.88) * mm, "end": v(41.86, -58.88) * mm});
            skLineSegment(sketch, "E29.8.1.0", {"start": v(37.23, -46.18) * mm, "end": v(37.23, -41.55) * mm});
            skLineSegment(sketch, "E29.8.1.1", {"start": v(37.23, -41.55) * mm, "end": v(41.86, -41.55) * mm});
            skLineSegment(sketch, "E29.8.1.2", {"start": v(41.86, -46.18) * mm, "end": v(41.86, -41.55) * mm});
            skLineSegment(sketch, "E29.8.1.3", {"start": v(37.23, -46.18) * mm, "end": v(41.86, -46.18) * mm});
            skLineSegment(sketch, "E29.8.2.0", {"start": v(37.23, -33.48) * mm, "end": v(37.23, -28.85) * mm});
            skLineSegment(sketch, "E29.8.2.1", {"start": v(37.23, -28.85) * mm, "end": v(41.86, -28.85) * mm});
            skLineSegment(sketch, "E29.8.2.2", {"start": v(41.86, -33.48) * mm, "end": v(41.86, -28.85) * mm});
            skLineSegment(sketch, "E29.8.2.3", {"start": v(37.23, -33.48) * mm, "end": v(41.86, -33.48) * mm});
            skLineSegment(sketch, "E29.direction1", {"start": v(-64.37, -58.88) * mm, "end": v(-51.67, -58.88) * mm, "construction": true});
            skLineSegment(sketch, "E29.direction2", {"start": v(-64.37, -58.88) * mm, "end": v(-64.37, -46.18) * mm, "construction": true});
            skSolve(sketch);
        }
        {
            var Q0;
            Q0=makeQuery(id+"F15.imprint","IMPRINT",FACE,{"disambiguationData":[TD([[makeQuery(id+"F15.imprint","IMPRINT",EDGE,{"derivedFrom":sQuery(id+"F15.wireOp",EDGE,"E28.bottom")}),1.0]])]});
            var Q1;
            Q1=makeQuery(id+"F15.imprint","IMPRINT",FACE,{"disambiguationData":[TD([[makeQuery(id+"F15.imprint","IMPRINT",EDGE,{"derivedFrom":sQuery(id+"F15.wireOp",EDGE,"E29.0.2.0")}),-1.0]])]});
            var Q2;
            Q2=makeQuery(id+"F15.imprint","IMPRINT",FACE,{"disambiguationData":[TD([[makeQuery(id+"F15.imprint","IMPRINT",EDGE,{"derivedFrom":sQuery(id+"F15.wireOp",EDGE,"E29.1.0.0")}),-1.0]])]});
            var Q3;
            Q3=makeQuery(id+"F15.imprint","IMPRINT",FACE,{"disambiguationData":[TD([[makeQuery(id+"F15.imprint","IMPRINT",EDGE,{"derivedFrom":sQuery(id+"F15.wireOp",EDGE,"E29.1.1.0")}),-1.0]])]});
            var Q4;
            Q4=makeQuery(id+"F15.imprint","IMPRINT",FACE,{"disambiguationData":[TD([[makeQuery(id+"F15.imprint","IMPRINT",EDGE,{"derivedFrom":sQuery(id+"F15.wireOp",EDGE,"E29.1.2.0")}),-1.0]])]});
            var Q5;
            Q5=makeQuery(id+"F15.imprint","IMPRINT",FACE,{"disambiguationData":[TD([[makeQuery(id+"F15.imprint","IMPRINT",EDGE,{"derivedFrom":sQuery(id+"F15.wireOp",EDGE,"E29.2.0.0")}),-1.0]])]});
            var Q6;
            Q6=makeQuery(id+"F15.imprint","IMPRINT",FACE,{"disambiguationData":[TD([[makeQuery(id+"F15.imprint","IMPRINT",EDGE,{"derivedFrom":sQuery(id+"F15.wireOp",EDGE,"E29.2.1.0")}),-1.0]])]});
            var Q7;
            Q7=makeQuery(id+"F15.imprint","IMPRINT",FACE,{"disambiguationData":[TD([[makeQuery(id+"F15.imprint","IMPRINT",EDGE,{"derivedFrom":sQuery(id+"F15.wireOp",EDGE,"E29.2.2.0")}),-1.0]])]});
            var Q8;
            Q8=makeQuery(id+"F15.imprint","IMPRINT",FACE,{"disambiguationData":[TD([[makeQuery(id+"F15.imprint","IMPRINT",EDGE,{"derivedFrom":sQuery(id+"F15.wireOp",EDGE,"E29.3.0.0")}),-1.0]])]});
            var Q9;
            Q9=makeQuery(id+"F15.imprint","IMPRINT",FACE,{"disambiguationData":[TD([[makeQuery(id+"F15.imprint","IMPRINT",EDGE,{"derivedFrom":sQuery(id+"F15.wireOp",EDGE,"E29.3.1.0")}),-1.0]])]});
            var Q10;
            Q10=makeQuery(id+"F15.imprint","IMPRINT",FACE,{"disambiguationData":[TD([[makeQuery(id+"F15.imprint","IMPRINT",EDGE,{"derivedFrom":sQuery(id+"F15.wireOp",EDGE,"E29.3.2.0")}),-1.0]])]});
            var Q11;
            Q11=makeQuery(id+"F15.imprint","IMPRINT",FACE,{"disambiguationData":[TD([[makeQuery(id+"F15.imprint","IMPRINT",EDGE,{"derivedFrom":sQuery(id+"F15.wireOp",EDGE,"E29.4.0.0")}),-1.0]])]});
            var Q12;
            Q12=makeQuery(id+"F15.imprint","IMPRINT",FACE,{"disambiguationData":[TD([[makeQuery(id+"F15.imprint","IMPRINT",EDGE,{"derivedFrom":sQuery(id+"F15.wireOp",EDGE,"E29.4.1.0")}),-1.0]])]});
            var Q13;
            Q13=makeQuery(id+"F15.imprint","IMPRINT",FACE,{"disambiguationData":[TD([[makeQuery(id+"F15.imprint","IMPRINT",EDGE,{"derivedFrom":sQuery(id+"F15.wireOp",EDGE,"E29.4.2.0")}),-1.0]])]});
            var Q14;
            Q14=makeQuery(id+"F15.imprint","IMPRINT",FACE,{"disambiguationData":[TD([[makeQuery(id+"F15.imprint","IMPRINT",EDGE,{"derivedFrom":sQuery(id+"F15.wireOp",EDGE,"E29.5.0.0")}),-1.0]])]});
            var Q15;
            Q15=makeQuery(id+"F15.imprint","IMPRINT",FACE,{"disambiguationData":[TD([[makeQuery(id+"F15.imprint","IMPRINT",EDGE,{"derivedFrom":sQuery(id+"F15.wireOp",EDGE,"E29.5.1.0")}),-1.0]])]});
            var Q16;
            Q16=makeQuery(id+"F15.imprint","IMPRINT",FACE,{"disambiguationData":[TD([[makeQuery(id+"F15.imprint","IMPRINT",EDGE,{"derivedFrom":sQuery(id+"F15.wireOp",EDGE,"E29.5.2.0")}),-1.0]])]});
            var Q17;
            Q17=makeQuery(id+"F15.imprint","IMPRINT",FACE,{"disambiguationData":[TD([[makeQuery(id+"F15.imprint","IMPRINT",EDGE,{"derivedFrom":sQuery(id+"F15.wireOp",EDGE,"E29.6.0.0")}),-1.0]])]});
            var Q18;
            Q18=makeQuery(id+"F15.imprint","IMPRINT",FACE,{"disambiguationData":[TD([[makeQuery(id+"F15.imprint","IMPRINT",EDGE,{"derivedFrom":sQuery(id+"F15.wireOp",EDGE,"E29.6.1.0")}),-1.0]])]});
            var Q19;
            Q19=makeQuery(id+"F15.imprint","IMPRINT",FACE,{"disambiguationData":[TD([[makeQuery(id+"F15.imprint","IMPRINT",EDGE,{"derivedFrom":sQuery(id+"F15.wireOp",EDGE,"E29.6.2.0")}),-1.0]])]});
            var Q20;
            Q20=makeQuery(id+"F15.imprint","IMPRINT",FACE,{"disambiguationData":[TD([[makeQuery(id+"F15.imprint","IMPRINT",EDGE,{"derivedFrom":sQuery(id+"F15.wireOp",EDGE,"E29.7.0.0")}),-1.0]])]});
            var Q21;
            Q21=makeQuery(id+"F15.imprint","IMPRINT",FACE,{"disambiguationData":[TD([[makeQuery(id+"F15.imprint","IMPRINT",EDGE,{"derivedFrom":sQuery(id+"F15.wireOp",EDGE,"E29.7.1.0")}),-1.0]])]});
            var Q22;
            Q22=makeQuery(id+"F15.imprint","IMPRINT",FACE,{"disambiguationData":[TD([[makeQuery(id+"F15.imprint","IMPRINT",EDGE,{"derivedFrom":sQuery(id+"F15.wireOp",EDGE,"E29.7.2.0")}),-1.0]])]});
            var Q23;
            Q23=makeQuery(id+"F15.imprint","IMPRINT",FACE,{"disambiguationData":[TD([[makeQuery(id+"F15.imprint","IMPRINT",EDGE,{"derivedFrom":sQuery(id+"F15.wireOp",EDGE,"E29.8.0.0")}),-1.0]])]});
            var Q24;
            Q24=makeQuery(id+"F15.imprint","IMPRINT",FACE,{"disambiguationData":[TD([[makeQuery(id+"F15.imprint","IMPRINT",EDGE,{"derivedFrom":sQuery(id+"F15.wireOp",EDGE,"E29.8.1.0")}),-1.0]])]});
            var Q25;
            Q25=makeQuery(id+"F15.imprint","IMPRINT",FACE,{"disambiguationData":[TD([[makeQuery(id+"F15.imprint","IMPRINT",EDGE,{"derivedFrom":sQuery(id+"F15.wireOp",EDGE,"E29.8.2.0")}),-1.0]])]});
            var Q26;
            Q26=makeQuery(id+"F15.imprint","IMPRINT",FACE,{"disambiguationData":[TD([[makeQuery(id+"F15.imprint","IMPRINT",EDGE,{"derivedFrom":sQuery(id+"F15.wireOp",EDGE,"E29.0.1.0")}),-1.0]])]});
            extrude(context, id + "F16", {"entities" : qUnion([Q0, Q1, Q2, Q3, Q4, Q5, Q6, Q7, Q8, Q9, Q10, Q11, Q12, Q13, Q14, Q15, Q16, Q17, Q18, Q19, Q20, Q21, Q22, Q23, Q24, Q25, Q26]), "operationType" : NewBodyOperationType.REMOVE, "endBound" : BoundingType.THROUGH_ALL, "oppositeDirection" : true, "depth" : 25.4 * mm});
        }
        {
            var Q0;
            Q0=makeQuery(id+"F1.opExtrude","SWEPT_FACE",FACE,{"disambiguationData":[OSD([sQuery(id+"F0.wireOp",EDGE,"E0.right")])]});
            var sketch = newSketch(context, id + "F17", { "sketchPlane" : qUnion([Q0])});
            skSolve(sketch);
        }
        {
            var Q0;
            Q0=makeQuery(id+"F14.boolean.opBoolean","MERGE",FACE,{"derivedFrom":[makeQuery(id+"F7.boolean.opBoolean","COPY",FACE,{"derivedFrom":makeQuery(id+"F7.opExtrude","SWEPT_FACE",FACE,{"disambiguationData":[OSD([sQuery(id+"F6.wireOp",EDGE,"E8.right")])]})}),makeQuery(id+"F14.opExtrude","SWEPT_FACE",FACE,{"disambiguationData":[OSD([sQuery(id+"F12.wireOp",EDGE,"E18")])]})]});
            var Q1;
            Q1=makeQuery(id+"F14.boolean.opBoolean","COPY",FACE,{"derivedFrom":makeQuery(id+"F14.opExtrude","SWEPT_FACE",FACE,{"disambiguationData":[OSD([sQuery(id+"F13.wireOp",EDGE,"E20")])]})});
            extrude(context, id + "F18", {"entities" : qUnion([Q0, Q1]), "operationType" : NewBodyOperationType.REMOVE, "oppositeDirection" : true, "depth" : 3.17 * mm});
        }
        {
            var Q0;
            Q0=makeQuery(id+"F14.boolean.opBoolean","MERGE",FACE,{"derivedFrom":[makeQuery(id+"F7.boolean.opBoolean","COPY",FACE,{"derivedFrom":makeQuery(id+"F7.opExtrude","SWEPT_FACE",FACE,{"disambiguationData":[OSD([sQuery(id+"F6.wireOp",EDGE,"E8.left")])]})}),makeQuery(id+"F14.opExtrude","SWEPT_FACE",FACE,{"disambiguationData":[OSD([sQuery(id+"F12.wireOp",EDGE,"E19")])]})]});
            var Q1;
            Q1=makeQuery(id+"F14.boolean.opBoolean","COPY",FACE,{"derivedFrom":makeQuery(id+"F14.opExtrude","SWEPT_FACE",FACE,{"disambiguationData":[OSD([sQuery(id+"F13.wireOp",EDGE,"E21")])]})});
            extrude(context, id + "F19", {"entities" : qUnion([Q0, Q1]), "operationType" : NewBodyOperationType.REMOVE, "oppositeDirection" : true, "depth" : 3.17 * mm});
        }
    });
